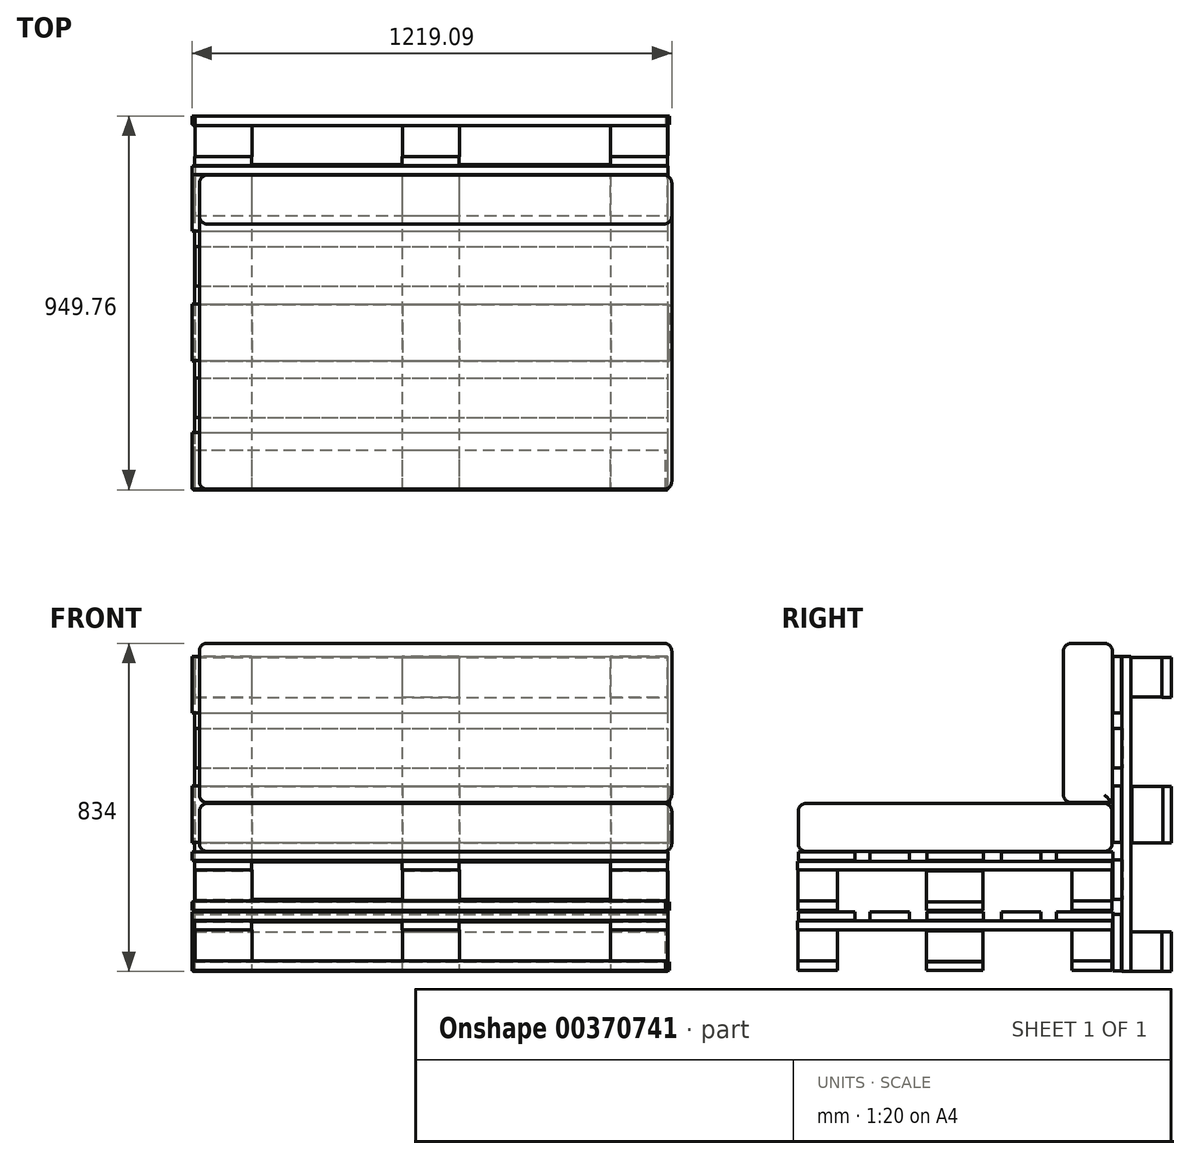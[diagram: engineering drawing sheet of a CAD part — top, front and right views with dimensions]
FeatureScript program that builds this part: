
annotation { "Feature Type Name" : "Feature", "Feature Type Description" : "" }
export const myFeature = defineFeature(function(context is Context, id is Id, definition is map)
    precondition{}
    {
        {
            var Q0;
            Q0=qCreatedBy(makeId("Top.planeOp"),FACE);
            var sketch = newSketch(context, id + "F0", { "sketchPlane" : qUnion([Q0])});
            skLineSegment(sketch, "E0.bottom", {"start": v(606.92, 402.88) * mm, "end": v(-606.52, 402.88) * mm, "construction": true});
            skLineSegment(sketch, "E0.top", {"start": v(606.92, -399.92) * mm, "end": v(-606.52, -399.92) * mm, "construction": true});
            skLineSegment(sketch, "E0.left", {"start": v(606.92, 402.88) * mm, "end": v(606.92, -399.92) * mm, "construction": true});
            skLineSegment(sketch, "E0.right", {"start": v(-606.52, 402.88) * mm, "end": v(-606.52, -399.92) * mm, "construction": true});
            skPoint(sketch, "E0.middle", {"position": v(0.2, 1.48) * mm});
            skSolve(sketch);
        }
        {
            var Q0;
            Q0=qCreatedBy(makeId("Right.planeOp"),FACE);
            var sketch = newSketch(context, id + "F1", { "sketchPlane" : qUnion([Q0])});
            skLineSegment(sketch, "E1.bottom", {"start": v(-398.91, 0) * mm, "end": v(-298, 0) * mm});
            skLineSegment(sketch, "E1.top", {"start": v(-398.91, 24.98) * mm, "end": v(-298, 24.98) * mm});
            skLineSegment(sketch, "E1.left", {"start": v(-398.91, 0) * mm, "end": v(-398.91, 24.98) * mm});
            skLineSegment(sketch, "E1.right", {"start": v(-298, 0) * mm, "end": v(-298, 24.98) * mm});
            skSolve(sketch);
        }
        {
            var Q0;
            Q0=makeQuery(id+"F1.imprint","IMPRINT",FACE,{"disambiguationData":[TD([[makeQuery(id+"F1.imprint","IMPRINT",EDGE,{"derivedFrom":sQuery(id+"F1.wireOp",EDGE,"E1.bottom")}),1.0]])]});
            extrude(context, id + "F2", {"entities" : qUnion([Q0]), "depth" : 600 * mm, "hasSecondDirection" : true, "secondDirectionOppositeDirection" : true, "secondDirectionDepth" : 600 * mm});
        }
        {
            var Q0;
            Q0=makeQuery(id+"F2.opExtrude","SWEPT_BODY",BODY,{"disambiguationData":[OSD([sQuery(id+"F1.wireOp",EDGE,"E1.bottom"),sQuery(id+"F1.wireOp",EDGE,"E1.top"),sQuery(id+"F1.wireOp",EDGE,"E1.left"),sQuery(id+"F1.wireOp",EDGE,"E1.right")])]});
            var Q1;
            Q1=qCreatedBy(makeId("Front.planeOp"),FACE);
            mirror(context, id + "F3", {"entities" : qUnion([Q0]), "mirrorPlane" : qUnion([Q1])});
        }
        {
            var Q0;
            Q0=qCreatedBy(makeId("Top.planeOp"),FACE);
            var sketch = newSketch(context, id + "F4", { "sketchPlane" : qUnion([Q0])});
            skLineSegment(sketch, "E2.bottom", {"start": v(604.9, 71.76) * mm, "end": v(-604.9, 71.76) * mm});
            skLineSegment(sketch, "E2.top", {"start": v(604.9, -71.76) * mm, "end": v(-604.9, -71.76) * mm});
            skLineSegment(sketch, "E2.left", {"start": v(604.9, 71.76) * mm, "end": v(604.9, -71.76) * mm});
            skLineSegment(sketch, "E2.right", {"start": v(-604.9, 71.76) * mm, "end": v(-604.9, -71.76) * mm});
            skPoint(sketch, "E2.middle", {"position": v(0, 0) * mm});
            skSolve(sketch);
        }
        {
            var Q0;
            Q0=makeQuery(id+"F4.imprint","IMPRINT",FACE,{"disambiguationData":[TD([[makeQuery(id+"F4.imprint","IMPRINT",EDGE,{"derivedFrom":sQuery(id+"F4.wireOp",EDGE,"E2.bottom")}),1.0]])]});
            extrude(context, id + "F5", {"entities" : qUnion([Q0]), "depth" : 22 * mm});
        }
        {
            var Q0;
            Q0=makeQuery(id+"F5.opExtrude","SWEPT_BODY",BODY,{"disambiguationData":[OSD([sQuery(id+"F4.wireOp",EDGE,"E2.bottom"),sQuery(id+"F4.wireOp",EDGE,"E2.top"),sQuery(id+"F4.wireOp",EDGE,"E2.left"),sQuery(id+"F4.wireOp",EDGE,"E2.right")])]});
            transform(context, id + "F6", {"entities" : qUnion([Q0]), "transformType" : TransformType.COPY});
        }
        {
            var Q0;
            Q0=qCreatedBy(makeId("Right.planeOp"),FACE);
            var sketch = newSketch(context, id + "F7", { "sketchPlane" : qUnion([Q0])});
            skLineSegment(sketch, "E3.bottom", {"start": v(398.94, 24.94) * mm, "end": v(297.72, 24.94) * mm});
            skLineSegment(sketch, "E3.top", {"start": v(398.94, 103.56) * mm, "end": v(297.72, 103.56) * mm});
            skLineSegment(sketch, "E3.left", {"start": v(398.94, 24.94) * mm, "end": v(398.94, 103.56) * mm});
            skLineSegment(sketch, "E3.right", {"start": v(297.72, 24.94) * mm, "end": v(297.72, 103.56) * mm});
            skSolve(sketch);
        }
        {
            var Q0;
            Q0=makeQuery(id+"F7.imprint","IMPRINT",FACE,{"disambiguationData":[TD([[makeQuery(id+"F7.imprint","IMPRINT",EDGE,{"derivedFrom":sQuery(id+"F7.wireOp",EDGE,"E3.bottom")}),-1.0]])]});
            extrude(context, id + "F8", {"entities" : qUnion([Q0]), "depth" : 145 * mm});
        }
        {
            var Q0;
            Q0=makeQuery(id+"F8.opExtrude","SWEPT_BODY",BODY,{"disambiguationData":[OSD([sQuery(id+"F7.wireOp",EDGE,"E3.bottom"),sQuery(id+"F7.wireOp",EDGE,"E3.top"),sQuery(id+"F7.wireOp",EDGE,"E3.left"),sQuery(id+"F7.wireOp",EDGE,"E3.right")])]});
            var Q1;
            Q1=sQuery(id+"F0.wireOp",EDGE,"E0.top");
            transform(context, id + "F9", {"entities" : qUnion([Q0]), "transformType" : TransformType.TRANSLATION_DISTANCE, "transformDirection" : qUnion([Q1]), "distance" : 455 * mm, "oppositeDirection" : true, "makeCopy" : false});
        }
        {
            var Q0;
            Q0=makeQuery(id+"F8.opExtrude","SWEPT_BODY",BODY,{"disambiguationData":[OSD([sQuery(id+"F7.wireOp",EDGE,"E3.bottom"),sQuery(id+"F7.wireOp",EDGE,"E3.top"),sQuery(id+"F7.wireOp",EDGE,"E3.left"),sQuery(id+"F7.wireOp",EDGE,"E3.right")])]});
            var Q1;
            Q1=makeQuery(id+"F3.opPattern","COPY",EDGE,{"derivedFrom":makeQuery(id+"F2.opExtrude","SWEPT_EDGE",EDGE,{"disambiguationData":[OSD([sQuery(id+"F1.wireOp",EDGE,"E1.top"),sQuery(id+"F1.wireOp",EDGE,"E1.left")])]}),"instanceName":"1"});
            transform(context, id + "F10", {"entities" : qUnion([Q0]), "transformType" : TransformType.TRANSLATION_DISTANCE, "transformDirection" : qUnion([Q1]), "distance" : 1055 * mm, "makeCopy" : true});
        }
        {
            var Q0;
            Q0=makeQuery(id+"F8.opExtrude","SWEPT_BODY",BODY,{"disambiguationData":[OSD([sQuery(id+"F7.wireOp",EDGE,"E3.bottom"),sQuery(id+"F7.wireOp",EDGE,"E3.top"),sQuery(id+"F7.wireOp",EDGE,"E3.left"),sQuery(id+"F7.wireOp",EDGE,"E3.right")])]});
            var Q1;
            Q1=makeQuery(id+"F3.opPattern","COPY",BODY,{"derivedFrom":makeQuery(id+"F2.opExtrude","SWEPT_BODY",BODY,{"disambiguationData":[OSD([sQuery(id+"F1.wireOp",EDGE,"E1.bottom"),sQuery(id+"F1.wireOp",EDGE,"E1.top"),sQuery(id+"F1.wireOp",EDGE,"E1.left"),sQuery(id+"F1.wireOp",EDGE,"E1.right")])]}),"instanceName":"1"});
            var Q2;
            Q2=makeQuery(id+"F3.opPattern","COPY",EDGE,{"derivedFrom":makeQuery(id+"F2.opExtrude","SWEPT_EDGE",EDGE,{"disambiguationData":[OSD([sQuery(id+"F1.wireOp",EDGE,"E1.top"),sQuery(id+"F1.wireOp",EDGE,"E1.left")])]}),"instanceName":"1"});
            transform(context, id + "F11", {"entities" : qUnion([Q0, Q1]), "transformType" : TransformType.TRANSLATION_DISTANCE, "transformDirection" : qUnion([Q2]), "distance" : 527 * mm, "makeCopy" : true});
        }
        {
            var Q0;
            Q0=makeQuery(id+"F11.opPattern","COPY",BODY,{"derivedFrom":makeQuery(id+"F3.opPattern","COPY",BODY,{"derivedFrom":makeQuery(id+"F2.opExtrude","SWEPT_BODY",BODY,{"disambiguationData":[OSD([sQuery(id+"F1.wireOp",EDGE,"E1.bottom"),sQuery(id+"F1.wireOp",EDGE,"E1.top"),sQuery(id+"F1.wireOp",EDGE,"E1.left"),sQuery(id+"F1.wireOp",EDGE,"E1.right")])]}),"instanceName":"1"}),"instanceName":"1"});
            deleteBodies(context, id + "F12", {"entities" : qUnion([Q0])});
        }
        {
            var Q0;
            Q0=makeQuery(id+"F8.opExtrude","SWEPT_BODY",BODY,{"disambiguationData":[OSD([sQuery(id+"F7.wireOp",EDGE,"E3.bottom"),sQuery(id+"F7.wireOp",EDGE,"E3.top"),sQuery(id+"F7.wireOp",EDGE,"E3.left"),sQuery(id+"F7.wireOp",EDGE,"E3.right")])]});
            var Q1;
            Q1=makeQuery(id+"F11.opPattern","COPY",BODY,{"derivedFrom":makeQuery(id+"F8.opExtrude","SWEPT_BODY",BODY,{"disambiguationData":[OSD([sQuery(id+"F7.wireOp",EDGE,"E3.bottom"),sQuery(id+"F7.wireOp",EDGE,"E3.top"),sQuery(id+"F7.wireOp",EDGE,"E3.left"),sQuery(id+"F7.wireOp",EDGE,"E3.right")])]}),"instanceName":"1"});
            var Q2;
            Q2=makeQuery(id+"F10.opPattern","COPY",BODY,{"derivedFrom":makeQuery(id+"F8.opExtrude","SWEPT_BODY",BODY,{"disambiguationData":[OSD([sQuery(id+"F7.wireOp",EDGE,"E3.bottom"),sQuery(id+"F7.wireOp",EDGE,"E3.top"),sQuery(id+"F7.wireOp",EDGE,"E3.left"),sQuery(id+"F7.wireOp",EDGE,"E3.right")])]}),"instanceName":"1"});
            var Q3;
            Q3=makeQuery(id+"F5.opExtrude","CAP_EDGE",EDGE,{"disambiguationData":[OSD([sQuery(id+"F4.wireOp",EDGE,"E2.right")])],"isStart":false});
            transform(context, id + "F13", {"entities" : qUnion([Q0, Q1, Q2]), "transformType" : TransformType.TRANSLATION_DISTANCE, "transformDirection" : qUnion([Q3]), "distance" : 697 * mm, "makeCopy" : true});
        }
        {
            var Q0;
            Q0=qCreatedBy(makeId("Right.planeOp"),FACE);
            var sketch = newSketch(context, id + "F14", { "sketchPlane" : qUnion([Q0])});
            skLineSegment(sketch, "E4.bottom", {"start": v(-71.96, 39.25) * mm, "end": v(71.96, 39.25) * mm});
            skLineSegment(sketch, "E4.top", {"start": v(-71.96, -39.25) * mm, "end": v(71.96, -39.25) * mm});
            skLineSegment(sketch, "E4.left", {"start": v(-71.96, 39.25) * mm, "end": v(-71.96, -39.25) * mm});
            skLineSegment(sketch, "E4.right", {"start": v(71.96, 39.25) * mm, "end": v(71.96, -39.25) * mm});
            skPoint(sketch, "E4.middle", {"position": v(0, 0) * mm});
            skSolve(sketch);
        }
        {
            var Q0;
            Q0=makeQuery(id+"F14.imprint","IMPRINT",FACE,{"disambiguationData":[TD([[makeQuery(id+"F14.imprint","IMPRINT",EDGE,{"derivedFrom":sQuery(id+"F14.wireOp",EDGE,"E4.bottom")}),-1.0]])]});
            extrude(context, id + "F15", {"entities" : qUnion([Q0]), "depth" : 145 * mm});
        }
        {
            var Q0;
            Q0=makeQuery(id+"F15.opExtrude","SWEPT_BODY",BODY,{"disambiguationData":[OSD([sQuery(id+"F14.wireOp",EDGE,"E4.bottom"),sQuery(id+"F14.wireOp",EDGE,"E4.top"),sQuery(id+"F14.wireOp",EDGE,"E4.left"),sQuery(id+"F14.wireOp",EDGE,"E4.right")])]});
            var Q1;
            Q1=makeQuery(id+"F13.opPattern","COPY",EDGE,{"derivedFrom":makeQuery(id+"F11.opPattern","COPY",EDGE,{"derivedFrom":makeQuery(id+"F8.opExtrude","CAP_EDGE",EDGE,{"disambiguationData":[OSD([sQuery(id+"F7.wireOp",EDGE,"E3.left")])],"isStart":false}),"instanceName":"1"}),"instanceName":"1"});
            transform(context, id + "F16", {"entities" : qUnion([Q0]), "transformType" : TransformType.TRANSLATION_DISTANCE, "transformDirection" : qUnion([Q1]), "distance" : 61.8 * mm, "makeCopy" : false});
        }
        {
            var Q0;
            Q0=makeQuery(id+"F15.opExtrude","SWEPT_BODY",BODY,{"disambiguationData":[OSD([sQuery(id+"F14.wireOp",EDGE,"E4.bottom"),sQuery(id+"F14.wireOp",EDGE,"E4.top"),sQuery(id+"F14.wireOp",EDGE,"E4.left"),sQuery(id+"F14.wireOp",EDGE,"E4.right")])]});
            var Q1;
            Q1=makeQuery(id+"F3.opPattern","COPY",BODY,{"derivedFrom":makeQuery(id+"F2.opExtrude","SWEPT_BODY",BODY,{"disambiguationData":[OSD([sQuery(id+"F1.wireOp",EDGE,"E1.bottom"),sQuery(id+"F1.wireOp",EDGE,"E1.top"),sQuery(id+"F1.wireOp",EDGE,"E1.left"),sQuery(id+"F1.wireOp",EDGE,"E1.right")])]}),"instanceName":"1"});
            var Q2;
            Q2=makeQuery(id+"F3.opPattern","COPY",EDGE,{"derivedFrom":makeQuery(id+"F2.opExtrude","SWEPT_EDGE",EDGE,{"disambiguationData":[OSD([sQuery(id+"F1.wireOp",EDGE,"E1.top"),sQuery(id+"F1.wireOp",EDGE,"E1.left")])]}),"instanceName":"1"});
            transform(context, id + "F17", {"entities" : qUnion([Q0, Q1]), "transformType" : TransformType.TRANSLATION_DISTANCE, "transformDirection" : qUnion([Q2]), "distance" : 72.6 * mm, "makeCopy" : false});
        }
        {
            var Q0;
            Q0=makeQuery(id+"F3.opPattern","COPY",BODY,{"derivedFrom":makeQuery(id+"F2.opExtrude","SWEPT_BODY",BODY,{"disambiguationData":[OSD([sQuery(id+"F1.wireOp",EDGE,"E1.bottom"),sQuery(id+"F1.wireOp",EDGE,"E1.top"),sQuery(id+"F1.wireOp",EDGE,"E1.left"),sQuery(id+"F1.wireOp",EDGE,"E1.right")])]}),"instanceName":"1"});
            var Q1;
            Q1=makeQuery(id+"F3.opPattern","COPY",EDGE,{"derivedFrom":makeQuery(id+"F2.opExtrude","SWEPT_EDGE",EDGE,{"disambiguationData":[OSD([sQuery(id+"F1.wireOp",EDGE,"E1.top"),sQuery(id+"F1.wireOp",EDGE,"E1.left")])]}),"instanceName":"1"});
            transform(context, id + "F18", {"entities" : qUnion([Q0]), "transformType" : TransformType.TRANSLATION_DISTANCE, "transformDirection" : qUnion([Q1]), "distance" : 77 * mm, "oppositeDirection" : true, "makeCopy" : false});
        }
        {
            var Q0;
            Q0=makeQuery(id+"F15.opExtrude","SWEPT_BODY",BODY,{"disambiguationData":[OSD([sQuery(id+"F14.wireOp",EDGE,"E4.bottom"),sQuery(id+"F14.wireOp",EDGE,"E4.top"),sQuery(id+"F14.wireOp",EDGE,"E4.left"),sQuery(id+"F14.wireOp",EDGE,"E4.right")])]});
            var Q1;
            Q1=makeQuery(id+"F5.opExtrude","CAP_EDGE",EDGE,{"disambiguationData":[OSD([sQuery(id+"F4.wireOp",EDGE,"E2.bottom")])],"isStart":false});
            transform(context, id + "F19", {"entities" : qUnion([Q0]), "transformType" : TransformType.TRANSLATION_DISTANCE, "transformDirection" : qUnion([Q1]), "distance" : 534 * mm, "oppositeDirection" : true, "makeCopy" : true});
        }
        {
            var Q0;
            Q0=makeQuery(id+"F15.opExtrude","SWEPT_BODY",BODY,{"disambiguationData":[OSD([sQuery(id+"F14.wireOp",EDGE,"E4.bottom"),sQuery(id+"F14.wireOp",EDGE,"E4.top"),sQuery(id+"F14.wireOp",EDGE,"E4.left"),sQuery(id+"F14.wireOp",EDGE,"E4.right")])]});
            var Q1;
            Q1=makeQuery(id+"F5.opExtrude","CAP_EDGE",EDGE,{"disambiguationData":[OSD([sQuery(id+"F4.wireOp",EDGE,"E2.bottom")])],"isStart":false});
            transform(context, id + "F20", {"entities" : qUnion([Q0]), "transformType" : TransformType.TRANSLATION_DISTANCE, "transformDirection" : qUnion([Q1]), "distance" : 532 * mm, "makeCopy" : true});
        }
        {
            var Q0;
            Q0=makeQuery(id+"F5.opExtrude","SWEPT_BODY",BODY,{"disambiguationData":[OSD([sQuery(id+"F4.wireOp",EDGE,"E2.bottom"),sQuery(id+"F4.wireOp",EDGE,"E2.top"),sQuery(id+"F4.wireOp",EDGE,"E2.left"),sQuery(id+"F4.wireOp",EDGE,"E2.right")])]});
            var Q1;
            Q1=makeQuery(id+"F20.opPattern","COPY",BODY,{"derivedFrom":makeQuery(id+"F15.opExtrude","SWEPT_BODY",BODY,{"disambiguationData":[OSD([sQuery(id+"F14.wireOp",EDGE,"E4.bottom"),sQuery(id+"F14.wireOp",EDGE,"E4.top"),sQuery(id+"F14.wireOp",EDGE,"E4.left"),sQuery(id+"F14.wireOp",EDGE,"E4.right")])]}),"instanceName":"1"});
            var Q2;
            Q2=makeQuery(id+"F2.opExtrude","SWEPT_EDGE",EDGE,{"disambiguationData":[OSD([sQuery(id+"F1.wireOp",EDGE,"E1.top"),sQuery(id+"F1.wireOp",EDGE,"E1.left")])]});
            transform(context, id + "F21", {"entities" : qUnion([Q0, Q1]), "transformType" : TransformType.TRANSLATION_DISTANCE, "transformDirection" : qUnion([Q2]), "distance" : 3 * mm, "oppositeDirection" : true, "makeCopy" : false});
        }
        {
            var Q0;
            Q0=qCreatedBy(makeId("Front.planeOp"),FACE);
            var sketch = newSketch(context, id + "F22", { "sketchPlane" : qUnion([Q0])});
            skLineSegment(sketch, "E5.bottom", {"start": v(-600.02, 103.6) * mm, "end": v(-455.57, 103.6) * mm});
            skLineSegment(sketch, "E5.top", {"start": v(-600.02, 125.7) * mm, "end": v(-455.57, 125.7) * mm});
            skLineSegment(sketch, "E5.left", {"start": v(-600.02, 103.6) * mm, "end": v(-600.02, 125.7) * mm});
            skLineSegment(sketch, "E5.right", {"start": v(-455.57, 103.6) * mm, "end": v(-455.57, 125.7) * mm});
            skSolve(sketch);
        }
        {
            var Q0;
            Q0=makeQuery(id+"F22.imprint","IMPRINT",FACE,{"disambiguationData":[TD([[makeQuery(id+"F22.imprint","IMPRINT",EDGE,{"derivedFrom":sQuery(id+"F22.wireOp",EDGE,"E5.bottom")}),1.0]])]});
            extrude(context, id + "F23", {"entities" : qUnion([Q0]), "depth" : 401 * mm, "hasSecondDirection" : true, "secondDirectionOppositeDirection" : true, "secondDirectionDepth" : 399 * mm});
        }
        {
            var Q0;
            Q0=makeQuery(id+"F23.opExtrude","SWEPT_BODY",BODY,{"disambiguationData":[OSD([sQuery(id+"F22.wireOp",EDGE,"E5.bottom"),sQuery(id+"F22.wireOp",EDGE,"E5.top"),sQuery(id+"F22.wireOp",EDGE,"E5.left"),sQuery(id+"F22.wireOp",EDGE,"E5.right")])]});
            var Q1;
            Q1=makeQuery(id+"F2.opExtrude","SWEPT_EDGE",EDGE,{"disambiguationData":[OSD([sQuery(id+"F1.wireOp",EDGE,"E1.top"),sQuery(id+"F1.wireOp",EDGE,"E1.left")])]});
            transform(context, id + "F24", {"entities" : qUnion([Q0]), "transformType" : TransformType.TRANSLATION_DISTANCE, "transformDirection" : qUnion([Q1]), "distance" : 529 * mm, "oppositeDirection" : true, "makeCopy" : true});
        }
        {
            var Q0;
            Q0=makeQuery(id+"F24.opPattern","COPY",BODY,{"derivedFrom":makeQuery(id+"F23.opExtrude","SWEPT_BODY",BODY,{"disambiguationData":[OSD([sQuery(id+"F22.wireOp",EDGE,"E5.bottom"),sQuery(id+"F22.wireOp",EDGE,"E5.top"),sQuery(id+"F22.wireOp",EDGE,"E5.left"),sQuery(id+"F22.wireOp",EDGE,"E5.right")])]}),"instanceName":"1"});
            var Q1;
            Q1=makeQuery(id+"F2.opExtrude","SWEPT_EDGE",EDGE,{"disambiguationData":[OSD([sQuery(id+"F1.wireOp",EDGE,"E1.top"),sQuery(id+"F1.wireOp",EDGE,"E1.left")])]});
            transform(context, id + "F25", {"entities" : qUnion([Q0]), "transformType" : TransformType.TRANSLATION_DISTANCE, "transformDirection" : qUnion([Q1]), "distance" : 527 * mm, "oppositeDirection" : true, "makeCopy" : true});
        }
        {
            var Q0;
            Q0=makeQuery(id+"F19.opPattern","COPY",BODY,{"derivedFrom":makeQuery(id+"F15.opExtrude","SWEPT_BODY",BODY,{"disambiguationData":[OSD([sQuery(id+"F14.wireOp",EDGE,"E4.bottom"),sQuery(id+"F14.wireOp",EDGE,"E4.top"),sQuery(id+"F14.wireOp",EDGE,"E4.left"),sQuery(id+"F14.wireOp",EDGE,"E4.right")])]}),"instanceName":"1"});
            var Q1;
            Q1=makeQuery(id+"F2.opExtrude","SWEPT_EDGE",EDGE,{"disambiguationData":[OSD([sQuery(id+"F1.wireOp",EDGE,"E1.top"),sQuery(id+"F1.wireOp",EDGE,"E1.left")])]});
            transform(context, id + "F26", {"entities" : qUnion([Q0]), "transformType" : TransformType.TRANSLATION_DISTANCE, "transformDirection" : qUnion([Q1]), "distance" : 7 * mm, "makeCopy" : false});
        }
        {
            var Q0;
            Q0=makeQuery(id+"F5.opExtrude","SWEPT_BODY",BODY,{"disambiguationData":[OSD([sQuery(id+"F4.wireOp",EDGE,"E2.bottom"),sQuery(id+"F4.wireOp",EDGE,"E2.top"),sQuery(id+"F4.wireOp",EDGE,"E2.left"),sQuery(id+"F4.wireOp",EDGE,"E2.right")])]});
            var Q1;
            Q1=makeQuery(id+"F19.opPattern","COPY",EDGE,{"derivedFrom":makeQuery(id+"F15.opExtrude","CAP_EDGE",EDGE,{"disambiguationData":[OSD([sQuery(id+"F14.wireOp",EDGE,"E4.left")])],"isStart":false}),"instanceName":"1"});
            transform(context, id + "F27", {"entities" : qUnion([Q0]), "transformType" : TransformType.TRANSLATION_DISTANCE, "transformDirection" : qUnion([Q1]), "distance" : 127 * mm, "oppositeDirection" : true, "makeCopy" : true});
        }
        {
            var Q0;
            Q0=makeQuery(id+"F27.opPattern","COPY",BODY,{"derivedFrom":makeQuery(id+"F5.opExtrude","SWEPT_BODY",BODY,{"disambiguationData":[OSD([sQuery(id+"F4.wireOp",EDGE,"E2.bottom"),sQuery(id+"F4.wireOp",EDGE,"E2.top"),sQuery(id+"F4.wireOp",EDGE,"E2.left"),sQuery(id+"F4.wireOp",EDGE,"E2.right")])]}),"instanceName":"1"});
            var Q1;
            Q1=makeQuery(id+"F25.opPattern","COPY",EDGE,{"derivedFrom":makeQuery(id+"F24.opPattern","COPY",EDGE,{"derivedFrom":makeQuery(id+"F23.opExtrude","SWEPT_EDGE",EDGE,{"disambiguationData":[OSD([sQuery(id+"F22.wireOp",EDGE,"E5.top"),sQuery(id+"F22.wireOp",EDGE,"E5.right")])]}),"instanceName":"1"}),"instanceName":"1"});
            transform(context, id + "F28", {"entities" : qUnion([Q0]), "transformType" : TransformType.TRANSLATION_DISTANCE, "transformDirection" : qUnion([Q1]), "distance" : 330 * mm, "oppositeDirection" : true, "makeCopy" : false});
        }
        {
            var Q0;
            Q0=makeQuery(id+"F27.opPattern","COPY",BODY,{"derivedFrom":makeQuery(id+"F5.opExtrude","SWEPT_BODY",BODY,{"disambiguationData":[OSD([sQuery(id+"F4.wireOp",EDGE,"E2.bottom"),sQuery(id+"F4.wireOp",EDGE,"E2.top"),sQuery(id+"F4.wireOp",EDGE,"E2.left"),sQuery(id+"F4.wireOp",EDGE,"E2.right")])]}),"instanceName":"1"});
            var Q1;
            Q1=makeQuery(id+"F25.opPattern","COPY",EDGE,{"derivedFrom":makeQuery(id+"F24.opPattern","COPY",EDGE,{"derivedFrom":makeQuery(id+"F23.opExtrude","SWEPT_EDGE",EDGE,{"disambiguationData":[OSD([sQuery(id+"F22.wireOp",EDGE,"E5.top"),sQuery(id+"F22.wireOp",EDGE,"E5.right")])]}),"instanceName":"1"}),"instanceName":"1"});
            transform(context, id + "F29", {"entities" : qUnion([Q0]), "transformType" : TransformType.TRANSLATION_DISTANCE, "transformDirection" : qUnion([Q1]), "distance" : 655 * mm, "makeCopy" : true});
        }
        {
            var Q0;
            Q0=makeQuery(id+"F29.opPattern","COPY",BODY,{"derivedFrom":makeQuery(id+"F27.opPattern","COPY",BODY,{"derivedFrom":makeQuery(id+"F5.opExtrude","SWEPT_BODY",BODY,{"disambiguationData":[OSD([sQuery(id+"F4.wireOp",EDGE,"E2.bottom"),sQuery(id+"F4.wireOp",EDGE,"E2.top"),sQuery(id+"F4.wireOp",EDGE,"E2.left"),sQuery(id+"F4.wireOp",EDGE,"E2.right")])]}),"instanceName":"1"}),"instanceName":"1"});
            var Q1;
            Q1=makeQuery(id+"F25.opPattern","COPY",EDGE,{"derivedFrom":makeQuery(id+"F24.opPattern","COPY",EDGE,{"derivedFrom":makeQuery(id+"F23.opExtrude","SWEPT_EDGE",EDGE,{"disambiguationData":[OSD([sQuery(id+"F22.wireOp",EDGE,"E5.top"),sQuery(id+"F22.wireOp",EDGE,"E5.right")])]}),"instanceName":"1"}),"instanceName":"1"});
            transform(context, id + "F30", {"entities" : qUnion([Q0]), "transformType" : TransformType.TRANSLATION_DISTANCE, "transformDirection" : qUnion([Q1]), "distance" : 326 * mm, "oppositeDirection" : true, "makeCopy" : true});
        }
        {
            var Q0;
            Q0=makeQuery(id+"F2.opExtrude","SWEPT_BODY",BODY,{"disambiguationData":[OSD([sQuery(id+"F1.wireOp",EDGE,"E1.bottom"),sQuery(id+"F1.wireOp",EDGE,"E1.top"),sQuery(id+"F1.wireOp",EDGE,"E1.left"),sQuery(id+"F1.wireOp",EDGE,"E1.right")])]});
            transform(context, id + "F31", {"entities" : qUnion([Q0]), "transformType" : TransformType.TRANSLATION_3D, "dx" : 0 * mm, "dy" : 180 * mm, "dz" : 125 * mm, "makeCopy" : true});
        }
        {
            var Q0;
            Q0=makeQuery(id+"F31.opPattern","COPY",BODY,{"derivedFrom":makeQuery(id+"F2.opExtrude","SWEPT_BODY",BODY,{"disambiguationData":[OSD([sQuery(id+"F1.wireOp",EDGE,"E1.bottom"),sQuery(id+"F1.wireOp",EDGE,"E1.top"),sQuery(id+"F1.wireOp",EDGE,"E1.left"),sQuery(id+"F1.wireOp",EDGE,"E1.right")])]}),"instanceName":"1"});
            var Q1;
            Q1=makeQuery(id+"F30.opPattern","COPY",EDGE,{"derivedFrom":makeQuery(id+"F29.opPattern","COPY",EDGE,{"derivedFrom":makeQuery(id+"F27.opPattern","COPY",EDGE,{"derivedFrom":makeQuery(id+"F5.opExtrude","SWEPT_EDGE",EDGE,{"disambiguationData":[OSD([sQuery(id+"F4.wireOp",EDGE,"E2.top"),sQuery(id+"F4.wireOp",EDGE,"E2.left")])]}),"instanceName":"1"}),"instanceName":"1"}),"instanceName":"1"});
            transform(context, id + "F32", {"entities" : qUnion([Q0]), "transformType" : TransformType.TRANSLATION_DISTANCE, "transformDirection" : qUnion([Q1]), "distance" : 1 * mm, "oppositeDirection" : true, "makeCopy" : false});
        }
        {
            var Q0;
            Q0=makeQuery(id+"F31.opPattern","COPY",BODY,{"derivedFrom":makeQuery(id+"F2.opExtrude","SWEPT_BODY",BODY,{"disambiguationData":[OSD([sQuery(id+"F1.wireOp",EDGE,"E1.bottom"),sQuery(id+"F1.wireOp",EDGE,"E1.top"),sQuery(id+"F1.wireOp",EDGE,"E1.left"),sQuery(id+"F1.wireOp",EDGE,"E1.right")])]}),"instanceName":"1"});
            var Q1;
            Q1=makeQuery(id+"F25.opPattern","COPY",EDGE,{"derivedFrom":makeQuery(id+"F24.opPattern","COPY",EDGE,{"derivedFrom":makeQuery(id+"F23.opExtrude","SWEPT_EDGE",EDGE,{"disambiguationData":[OSD([sQuery(id+"F22.wireOp",EDGE,"E5.top"),sQuery(id+"F22.wireOp",EDGE,"E5.right")])]}),"instanceName":"1"}),"instanceName":"1"});
            transform(context, id + "F33", {"entities" : qUnion([Q0]), "transformType" : TransformType.TRANSLATION_DISTANCE, "transformDirection" : qUnion([Q1]), "distance" : 334 * mm, "makeCopy" : true});
        }
        {
            var Q0;
            Q0=makeQuery(id+"F31.opPattern","COPY",BODY,{"derivedFrom":makeQuery(id+"F2.opExtrude","SWEPT_BODY",BODY,{"disambiguationData":[OSD([sQuery(id+"F1.wireOp",EDGE,"E1.bottom"),sQuery(id+"F1.wireOp",EDGE,"E1.top"),sQuery(id+"F1.wireOp",EDGE,"E1.left"),sQuery(id+"F1.wireOp",EDGE,"E1.right")])]}),"instanceName":"1"});
            var Q1;
            Q1=makeQuery(id+"F33.opPattern","COPY",BODY,{"derivedFrom":makeQuery(id+"F31.opPattern","COPY",BODY,{"derivedFrom":makeQuery(id+"F2.opExtrude","SWEPT_BODY",BODY,{"disambiguationData":[OSD([sQuery(id+"F1.wireOp",EDGE,"E1.bottom"),sQuery(id+"F1.wireOp",EDGE,"E1.top"),sQuery(id+"F1.wireOp",EDGE,"E1.left"),sQuery(id+"F1.wireOp",EDGE,"E1.right")])]}),"instanceName":"1"}),"instanceName":"1"});
            var Q2;
            Q2=makeQuery(id+"F30.opPattern","COPY",EDGE,{"derivedFrom":makeQuery(id+"F29.opPattern","COPY",EDGE,{"derivedFrom":makeQuery(id+"F27.opPattern","COPY",EDGE,{"derivedFrom":makeQuery(id+"F5.opExtrude","SWEPT_EDGE",EDGE,{"disambiguationData":[OSD([sQuery(id+"F4.wireOp",EDGE,"E2.bottom"),sQuery(id+"F4.wireOp",EDGE,"E2.left")])]}),"instanceName":"1"}),"instanceName":"1"}),"instanceName":"1"});
            transform(context, id + "F34", {"entities" : qUnion([Q0, Q1]), "transformType" : TransformType.TRANSLATION_DISTANCE, "transformDirection" : qUnion([Q2]), "distance" : 2 * mm, "makeCopy" : false});
        }
        {
            var Q0;
            Q0=makeQuery(id+"F2.opExtrude","SWEPT_BODY",BODY,{"disambiguationData":[OSD([sQuery(id+"F1.wireOp",EDGE,"E1.bottom"),sQuery(id+"F1.wireOp",EDGE,"E1.top"),sQuery(id+"F1.wireOp",EDGE,"E1.left"),sQuery(id+"F1.wireOp",EDGE,"E1.right")])]});
            var Q1;
            Q1=makeQuery(id+"F3.opPattern","COPY",BODY,{"derivedFrom":makeQuery(id+"F2.opExtrude","SWEPT_BODY",BODY,{"disambiguationData":[OSD([sQuery(id+"F1.wireOp",EDGE,"E1.bottom"),sQuery(id+"F1.wireOp",EDGE,"E1.top"),sQuery(id+"F1.wireOp",EDGE,"E1.left"),sQuery(id+"F1.wireOp",EDGE,"E1.right")])]}),"instanceName":"1"});
            var Q2;
            Q2=makeQuery(id+"F25.opPattern","COPY",BODY,{"derivedFrom":makeQuery(id+"F24.opPattern","COPY",BODY,{"derivedFrom":makeQuery(id+"F23.opExtrude","SWEPT_BODY",BODY,{"disambiguationData":[OSD([sQuery(id+"F22.wireOp",EDGE,"E5.bottom"),sQuery(id+"F22.wireOp",EDGE,"E5.top"),sQuery(id+"F22.wireOp",EDGE,"E5.left"),sQuery(id+"F22.wireOp",EDGE,"E5.right")])]}),"instanceName":"1"}),"instanceName":"1"});
            var Q3;
            Q3=makeQuery(id+"F13.opPattern","COPY",BODY,{"derivedFrom":makeQuery(id+"F8.opExtrude","SWEPT_BODY",BODY,{"disambiguationData":[OSD([sQuery(id+"F7.wireOp",EDGE,"E3.bottom"),sQuery(id+"F7.wireOp",EDGE,"E3.top"),sQuery(id+"F7.wireOp",EDGE,"E3.left"),sQuery(id+"F7.wireOp",EDGE,"E3.right")])]}),"instanceName":"1"});
            var Q4;
            Q4=makeQuery(id+"F27.opPattern","COPY",BODY,{"derivedFrom":makeQuery(id+"F5.opExtrude","SWEPT_BODY",BODY,{"disambiguationData":[OSD([sQuery(id+"F4.wireOp",EDGE,"E2.bottom"),sQuery(id+"F4.wireOp",EDGE,"E2.top"),sQuery(id+"F4.wireOp",EDGE,"E2.left"),sQuery(id+"F4.wireOp",EDGE,"E2.right")])]}),"instanceName":"1"});
            var Q5;
            Q5=makeQuery(id+"F8.opExtrude","SWEPT_BODY",BODY,{"disambiguationData":[OSD([sQuery(id+"F7.wireOp",EDGE,"E3.bottom"),sQuery(id+"F7.wireOp",EDGE,"E3.top"),sQuery(id+"F7.wireOp",EDGE,"E3.left"),sQuery(id+"F7.wireOp",EDGE,"E3.right")])]});
            var Q6;
            Q6=makeQuery(id+"F5.opExtrude","SWEPT_BODY",BODY,{"disambiguationData":[OSD([sQuery(id+"F4.wireOp",EDGE,"E2.bottom"),sQuery(id+"F4.wireOp",EDGE,"E2.top"),sQuery(id+"F4.wireOp",EDGE,"E2.left"),sQuery(id+"F4.wireOp",EDGE,"E2.right")])]});
            var Q7;
            Q7=makeQuery(id+"F31.opPattern","COPY",BODY,{"derivedFrom":makeQuery(id+"F2.opExtrude","SWEPT_BODY",BODY,{"disambiguationData":[OSD([sQuery(id+"F1.wireOp",EDGE,"E1.bottom"),sQuery(id+"F1.wireOp",EDGE,"E1.top"),sQuery(id+"F1.wireOp",EDGE,"E1.left"),sQuery(id+"F1.wireOp",EDGE,"E1.right")])]}),"instanceName":"1"});
            var Q8;
            Q8=makeQuery(id+"F29.opPattern","COPY",BODY,{"derivedFrom":makeQuery(id+"F27.opPattern","COPY",BODY,{"derivedFrom":makeQuery(id+"F5.opExtrude","SWEPT_BODY",BODY,{"disambiguationData":[OSD([sQuery(id+"F4.wireOp",EDGE,"E2.bottom"),sQuery(id+"F4.wireOp",EDGE,"E2.top"),sQuery(id+"F4.wireOp",EDGE,"E2.left"),sQuery(id+"F4.wireOp",EDGE,"E2.right")])]}),"instanceName":"1"}),"instanceName":"1"});
            var Q9;
            Q9=makeQuery(id+"F19.opPattern","COPY",BODY,{"derivedFrom":makeQuery(id+"F15.opExtrude","SWEPT_BODY",BODY,{"disambiguationData":[OSD([sQuery(id+"F14.wireOp",EDGE,"E4.bottom"),sQuery(id+"F14.wireOp",EDGE,"E4.top"),sQuery(id+"F14.wireOp",EDGE,"E4.left"),sQuery(id+"F14.wireOp",EDGE,"E4.right")])]}),"instanceName":"1"});
            var Q10;
            Q10=makeQuery(id+"F30.opPattern","COPY",BODY,{"derivedFrom":makeQuery(id+"F29.opPattern","COPY",BODY,{"derivedFrom":makeQuery(id+"F27.opPattern","COPY",BODY,{"derivedFrom":makeQuery(id+"F5.opExtrude","SWEPT_BODY",BODY,{"disambiguationData":[OSD([sQuery(id+"F4.wireOp",EDGE,"E2.bottom"),sQuery(id+"F4.wireOp",EDGE,"E2.top"),sQuery(id+"F4.wireOp",EDGE,"E2.left"),sQuery(id+"F4.wireOp",EDGE,"E2.right")])]}),"instanceName":"1"}),"instanceName":"1"}),"instanceName":"1"});
            var Q11;
            Q11=makeQuery(id+"F33.opPattern","COPY",BODY,{"derivedFrom":makeQuery(id+"F31.opPattern","COPY",BODY,{"derivedFrom":makeQuery(id+"F2.opExtrude","SWEPT_BODY",BODY,{"disambiguationData":[OSD([sQuery(id+"F1.wireOp",EDGE,"E1.bottom"),sQuery(id+"F1.wireOp",EDGE,"E1.top"),sQuery(id+"F1.wireOp",EDGE,"E1.left"),sQuery(id+"F1.wireOp",EDGE,"E1.right")])]}),"instanceName":"1"}),"instanceName":"1"});
            var Q12;
            Q12=makeQuery(id+"F6.opPattern","COPY",BODY,{"derivedFrom":makeQuery(id+"F5.opExtrude","SWEPT_BODY",BODY,{"disambiguationData":[OSD([sQuery(id+"F4.wireOp",EDGE,"E2.bottom"),sQuery(id+"F4.wireOp",EDGE,"E2.top"),sQuery(id+"F4.wireOp",EDGE,"E2.left"),sQuery(id+"F4.wireOp",EDGE,"E2.right")])]}),"instanceName":"1"});
            var Q13;
            Q13=makeQuery(id+"F24.opPattern","COPY",BODY,{"derivedFrom":makeQuery(id+"F23.opExtrude","SWEPT_BODY",BODY,{"disambiguationData":[OSD([sQuery(id+"F22.wireOp",EDGE,"E5.bottom"),sQuery(id+"F22.wireOp",EDGE,"E5.top"),sQuery(id+"F22.wireOp",EDGE,"E5.left"),sQuery(id+"F22.wireOp",EDGE,"E5.right")])]}),"instanceName":"1"});
            var Q14;
            Q14=makeQuery(id+"F15.opExtrude","SWEPT_BODY",BODY,{"disambiguationData":[OSD([sQuery(id+"F14.wireOp",EDGE,"E4.bottom"),sQuery(id+"F14.wireOp",EDGE,"E4.top"),sQuery(id+"F14.wireOp",EDGE,"E4.left"),sQuery(id+"F14.wireOp",EDGE,"E4.right")])]});
            var Q15;
            Q15=makeQuery(id+"F13.opPattern","COPY",BODY,{"derivedFrom":makeQuery(id+"F11.opPattern","COPY",BODY,{"derivedFrom":makeQuery(id+"F8.opExtrude","SWEPT_BODY",BODY,{"disambiguationData":[OSD([sQuery(id+"F7.wireOp",EDGE,"E3.bottom"),sQuery(id+"F7.wireOp",EDGE,"E3.top"),sQuery(id+"F7.wireOp",EDGE,"E3.left"),sQuery(id+"F7.wireOp",EDGE,"E3.right")])]}),"instanceName":"1"}),"instanceName":"1"});
            var Q16;
            Q16=makeQuery(id+"F11.opPattern","COPY",BODY,{"derivedFrom":makeQuery(id+"F8.opExtrude","SWEPT_BODY",BODY,{"disambiguationData":[OSD([sQuery(id+"F7.wireOp",EDGE,"E3.bottom"),sQuery(id+"F7.wireOp",EDGE,"E3.top"),sQuery(id+"F7.wireOp",EDGE,"E3.left"),sQuery(id+"F7.wireOp",EDGE,"E3.right")])]}),"instanceName":"1"});
            var Q17;
            Q17=makeQuery(id+"F20.opPattern","COPY",BODY,{"derivedFrom":makeQuery(id+"F15.opExtrude","SWEPT_BODY",BODY,{"disambiguationData":[OSD([sQuery(id+"F14.wireOp",EDGE,"E4.bottom"),sQuery(id+"F14.wireOp",EDGE,"E4.top"),sQuery(id+"F14.wireOp",EDGE,"E4.left"),sQuery(id+"F14.wireOp",EDGE,"E4.right")])]}),"instanceName":"1"});
            var Q18;
            Q18=makeQuery(id+"F13.opPattern","COPY",BODY,{"derivedFrom":makeQuery(id+"F10.opPattern","COPY",BODY,{"derivedFrom":makeQuery(id+"F8.opExtrude","SWEPT_BODY",BODY,{"disambiguationData":[OSD([sQuery(id+"F7.wireOp",EDGE,"E3.bottom"),sQuery(id+"F7.wireOp",EDGE,"E3.top"),sQuery(id+"F7.wireOp",EDGE,"E3.left"),sQuery(id+"F7.wireOp",EDGE,"E3.right")])]}),"instanceName":"1"}),"instanceName":"1"});
            var Q19;
            Q19=makeQuery(id+"F23.opExtrude","SWEPT_BODY",BODY,{"disambiguationData":[OSD([sQuery(id+"F22.wireOp",EDGE,"E5.bottom"),sQuery(id+"F22.wireOp",EDGE,"E5.top"),sQuery(id+"F22.wireOp",EDGE,"E5.left"),sQuery(id+"F22.wireOp",EDGE,"E5.right")])]});
            var Q20;
            Q20=makeQuery(id+"F10.opPattern","COPY",BODY,{"derivedFrom":makeQuery(id+"F8.opExtrude","SWEPT_BODY",BODY,{"disambiguationData":[OSD([sQuery(id+"F7.wireOp",EDGE,"E3.bottom"),sQuery(id+"F7.wireOp",EDGE,"E3.top"),sQuery(id+"F7.wireOp",EDGE,"E3.left"),sQuery(id+"F7.wireOp",EDGE,"E3.right")])]}),"instanceName":"1"});
            var Q21;
            Q21=makeQuery(id+"F27.opPattern","COPY",EDGE,{"derivedFrom":makeQuery(id+"F5.opExtrude","CAP_EDGE",EDGE,{"disambiguationData":[OSD([sQuery(id+"F4.wireOp",EDGE,"E2.top")])],"isStart":false}),"instanceName":"1"});
            transform(context, id + "F35", {"entities" : qUnion([Q0, Q1, Q2, Q3, Q4, Q5, Q6, Q7, Q8, Q9, Q10, Q11, Q12, Q13, Q14, Q15, Q16, Q17, Q18, Q19, Q20]), "transformType" : TransformType.ROTATION, "transformAxis" : qUnion([Q21]), "angle" : 90 * degree, "makeCopy" : true});
        }
        {
            var Q0;
            Q0=makeQuery(id+"F35.opPattern","COPY",EDGE,{"derivedFrom":makeQuery(id+"F5.opExtrude","CAP_EDGE",EDGE,{"disambiguationData":[OSD([sQuery(id+"F4.wireOp",EDGE,"E2.left")])],"isStart":true}),"instanceName":"1"});
            cPoint(context, id + "F36", {"entities" : qUnion([Q0]), "parameter" : 0.5});
        }
        {
            var Q0;
            Q0=makeQuery(id+"F35.opPattern","COPY",BODY,{"derivedFrom":makeQuery(id+"F31.opPattern","COPY",BODY,{"derivedFrom":makeQuery(id+"F2.opExtrude","SWEPT_BODY",BODY,{"disambiguationData":[OSD([sQuery(id+"F1.wireOp",EDGE,"E1.bottom"),sQuery(id+"F1.wireOp",EDGE,"E1.top"),sQuery(id+"F1.wireOp",EDGE,"E1.left"),sQuery(id+"F1.wireOp",EDGE,"E1.right")])]}),"instanceName":"1"}),"instanceName":"1"});
            var Q1;
            Q1=makeQuery(id+"F35.opPattern","COPY",BODY,{"derivedFrom":makeQuery(id+"F25.opPattern","COPY",BODY,{"derivedFrom":makeQuery(id+"F24.opPattern","COPY",BODY,{"derivedFrom":makeQuery(id+"F23.opExtrude","SWEPT_BODY",BODY,{"disambiguationData":[OSD([sQuery(id+"F22.wireOp",EDGE,"E5.bottom"),sQuery(id+"F22.wireOp",EDGE,"E5.top"),sQuery(id+"F22.wireOp",EDGE,"E5.left"),sQuery(id+"F22.wireOp",EDGE,"E5.right")])]}),"instanceName":"1"}),"instanceName":"1"}),"instanceName":"1"});
            var Q2;
            Q2=makeQuery(id+"F35.opPattern","COPY",BODY,{"derivedFrom":makeQuery(id+"F27.opPattern","COPY",BODY,{"derivedFrom":makeQuery(id+"F5.opExtrude","SWEPT_BODY",BODY,{"disambiguationData":[OSD([sQuery(id+"F4.wireOp",EDGE,"E2.bottom"),sQuery(id+"F4.wireOp",EDGE,"E2.top"),sQuery(id+"F4.wireOp",EDGE,"E2.left"),sQuery(id+"F4.wireOp",EDGE,"E2.right")])]}),"instanceName":"1"}),"instanceName":"1"});
            var Q3;
            Q3=makeQuery(id+"F35.opPattern","COPY",BODY,{"derivedFrom":makeQuery(id+"F2.opExtrude","SWEPT_BODY",BODY,{"disambiguationData":[OSD([sQuery(id+"F1.wireOp",EDGE,"E1.bottom"),sQuery(id+"F1.wireOp",EDGE,"E1.top"),sQuery(id+"F1.wireOp",EDGE,"E1.left"),sQuery(id+"F1.wireOp",EDGE,"E1.right")])]}),"instanceName":"1"});
            var Q4;
            Q4=makeQuery(id+"F35.opPattern","COPY",BODY,{"derivedFrom":makeQuery(id+"F13.opPattern","COPY",BODY,{"derivedFrom":makeQuery(id+"F8.opExtrude","SWEPT_BODY",BODY,{"disambiguationData":[OSD([sQuery(id+"F7.wireOp",EDGE,"E3.bottom"),sQuery(id+"F7.wireOp",EDGE,"E3.top"),sQuery(id+"F7.wireOp",EDGE,"E3.left"),sQuery(id+"F7.wireOp",EDGE,"E3.right")])]}),"instanceName":"1"}),"instanceName":"1"});
            var Q5;
            Q5=makeQuery(id+"F35.opPattern","COPY",BODY,{"derivedFrom":makeQuery(id+"F13.opPattern","COPY",BODY,{"derivedFrom":makeQuery(id+"F11.opPattern","COPY",BODY,{"derivedFrom":makeQuery(id+"F8.opExtrude","SWEPT_BODY",BODY,{"disambiguationData":[OSD([sQuery(id+"F7.wireOp",EDGE,"E3.bottom"),sQuery(id+"F7.wireOp",EDGE,"E3.top"),sQuery(id+"F7.wireOp",EDGE,"E3.left"),sQuery(id+"F7.wireOp",EDGE,"E3.right")])]}),"instanceName":"1"}),"instanceName":"1"}),"instanceName":"1"});
            var Q6;
            Q6=makeQuery(id+"F35.opPattern","COPY",BODY,{"derivedFrom":makeQuery(id+"F24.opPattern","COPY",BODY,{"derivedFrom":makeQuery(id+"F23.opExtrude","SWEPT_BODY",BODY,{"disambiguationData":[OSD([sQuery(id+"F22.wireOp",EDGE,"E5.bottom"),sQuery(id+"F22.wireOp",EDGE,"E5.top"),sQuery(id+"F22.wireOp",EDGE,"E5.left"),sQuery(id+"F22.wireOp",EDGE,"E5.right")])]}),"instanceName":"1"}),"instanceName":"1"});
            var Q7;
            Q7=makeQuery(id+"F35.opPattern","COPY",BODY,{"derivedFrom":makeQuery(id+"F13.opPattern","COPY",BODY,{"derivedFrom":makeQuery(id+"F10.opPattern","COPY",BODY,{"derivedFrom":makeQuery(id+"F8.opExtrude","SWEPT_BODY",BODY,{"disambiguationData":[OSD([sQuery(id+"F7.wireOp",EDGE,"E3.bottom"),sQuery(id+"F7.wireOp",EDGE,"E3.top"),sQuery(id+"F7.wireOp",EDGE,"E3.left"),sQuery(id+"F7.wireOp",EDGE,"E3.right")])]}),"instanceName":"1"}),"instanceName":"1"}),"instanceName":"1"});
            var Q8;
            Q8=makeQuery(id+"F35.opPattern","COPY",BODY,{"derivedFrom":makeQuery(id+"F23.opExtrude","SWEPT_BODY",BODY,{"disambiguationData":[OSD([sQuery(id+"F22.wireOp",EDGE,"E5.bottom"),sQuery(id+"F22.wireOp",EDGE,"E5.top"),sQuery(id+"F22.wireOp",EDGE,"E5.left"),sQuery(id+"F22.wireOp",EDGE,"E5.right")])]}),"instanceName":"1"});
            var Q9;
            Q9=makeQuery(id+"F35.opPattern","COPY",BODY,{"derivedFrom":makeQuery(id+"F29.opPattern","COPY",BODY,{"derivedFrom":makeQuery(id+"F27.opPattern","COPY",BODY,{"derivedFrom":makeQuery(id+"F5.opExtrude","SWEPT_BODY",BODY,{"disambiguationData":[OSD([sQuery(id+"F4.wireOp",EDGE,"E2.bottom"),sQuery(id+"F4.wireOp",EDGE,"E2.top"),sQuery(id+"F4.wireOp",EDGE,"E2.left"),sQuery(id+"F4.wireOp",EDGE,"E2.right")])]}),"instanceName":"1"}),"instanceName":"1"}),"instanceName":"1"});
            var Q10;
            Q10=makeQuery(id+"F35.opPattern","COPY",BODY,{"derivedFrom":makeQuery(id+"F30.opPattern","COPY",BODY,{"derivedFrom":makeQuery(id+"F29.opPattern","COPY",BODY,{"derivedFrom":makeQuery(id+"F27.opPattern","COPY",BODY,{"derivedFrom":makeQuery(id+"F5.opExtrude","SWEPT_BODY",BODY,{"disambiguationData":[OSD([sQuery(id+"F4.wireOp",EDGE,"E2.bottom"),sQuery(id+"F4.wireOp",EDGE,"E2.top"),sQuery(id+"F4.wireOp",EDGE,"E2.left"),sQuery(id+"F4.wireOp",EDGE,"E2.right")])]}),"instanceName":"1"}),"instanceName":"1"}),"instanceName":"1"}),"instanceName":"1"});
            var Q11;
            Q11=makeQuery(id+"F35.opPattern","COPY",BODY,{"derivedFrom":makeQuery(id+"F33.opPattern","COPY",BODY,{"derivedFrom":makeQuery(id+"F31.opPattern","COPY",BODY,{"derivedFrom":makeQuery(id+"F2.opExtrude","SWEPT_BODY",BODY,{"disambiguationData":[OSD([sQuery(id+"F1.wireOp",EDGE,"E1.bottom"),sQuery(id+"F1.wireOp",EDGE,"E1.top"),sQuery(id+"F1.wireOp",EDGE,"E1.left"),sQuery(id+"F1.wireOp",EDGE,"E1.right")])]}),"instanceName":"1"}),"instanceName":"1"}),"instanceName":"1"});
            var Q12;
            Q12=makeQuery(id+"F35.opPattern","COPY",BODY,{"derivedFrom":makeQuery(id+"F19.opPattern","COPY",BODY,{"derivedFrom":makeQuery(id+"F15.opExtrude","SWEPT_BODY",BODY,{"disambiguationData":[OSD([sQuery(id+"F14.wireOp",EDGE,"E4.bottom"),sQuery(id+"F14.wireOp",EDGE,"E4.top"),sQuery(id+"F14.wireOp",EDGE,"E4.left"),sQuery(id+"F14.wireOp",EDGE,"E4.right")])]}),"instanceName":"1"}),"instanceName":"1"});
            var Q13;
            Q13=makeQuery(id+"F35.opPattern","COPY",BODY,{"derivedFrom":makeQuery(id+"F8.opExtrude","SWEPT_BODY",BODY,{"disambiguationData":[OSD([sQuery(id+"F7.wireOp",EDGE,"E3.bottom"),sQuery(id+"F7.wireOp",EDGE,"E3.top"),sQuery(id+"F7.wireOp",EDGE,"E3.left"),sQuery(id+"F7.wireOp",EDGE,"E3.right")])]}),"instanceName":"1"});
            var Q14;
            Q14=makeQuery(id+"F35.opPattern","COPY",BODY,{"derivedFrom":makeQuery(id+"F5.opExtrude","SWEPT_BODY",BODY,{"disambiguationData":[OSD([sQuery(id+"F4.wireOp",EDGE,"E2.bottom"),sQuery(id+"F4.wireOp",EDGE,"E2.top"),sQuery(id+"F4.wireOp",EDGE,"E2.left"),sQuery(id+"F4.wireOp",EDGE,"E2.right")])]}),"instanceName":"1"});
            var Q15;
            Q15=makeQuery(id+"F35.opPattern","COPY",BODY,{"derivedFrom":makeQuery(id+"F3.opPattern","COPY",BODY,{"derivedFrom":makeQuery(id+"F2.opExtrude","SWEPT_BODY",BODY,{"disambiguationData":[OSD([sQuery(id+"F1.wireOp",EDGE,"E1.bottom"),sQuery(id+"F1.wireOp",EDGE,"E1.top"),sQuery(id+"F1.wireOp",EDGE,"E1.left"),sQuery(id+"F1.wireOp",EDGE,"E1.right")])]}),"instanceName":"1"}),"instanceName":"1"});
            var Q16;
            Q16=makeQuery(id+"F35.opPattern","COPY",BODY,{"derivedFrom":makeQuery(id+"F6.opPattern","COPY",BODY,{"derivedFrom":makeQuery(id+"F5.opExtrude","SWEPT_BODY",BODY,{"disambiguationData":[OSD([sQuery(id+"F4.wireOp",EDGE,"E2.bottom"),sQuery(id+"F4.wireOp",EDGE,"E2.top"),sQuery(id+"F4.wireOp",EDGE,"E2.left"),sQuery(id+"F4.wireOp",EDGE,"E2.right")])]}),"instanceName":"1"}),"instanceName":"1"});
            var Q17;
            Q17=makeQuery(id+"F35.opPattern","COPY",BODY,{"derivedFrom":makeQuery(id+"F15.opExtrude","SWEPT_BODY",BODY,{"disambiguationData":[OSD([sQuery(id+"F14.wireOp",EDGE,"E4.bottom"),sQuery(id+"F14.wireOp",EDGE,"E4.top"),sQuery(id+"F14.wireOp",EDGE,"E4.left"),sQuery(id+"F14.wireOp",EDGE,"E4.right")])]}),"instanceName":"1"});
            var Q18;
            Q18=makeQuery(id+"F35.opPattern","COPY",BODY,{"derivedFrom":makeQuery(id+"F11.opPattern","COPY",BODY,{"derivedFrom":makeQuery(id+"F8.opExtrude","SWEPT_BODY",BODY,{"disambiguationData":[OSD([sQuery(id+"F7.wireOp",EDGE,"E3.bottom"),sQuery(id+"F7.wireOp",EDGE,"E3.top"),sQuery(id+"F7.wireOp",EDGE,"E3.left"),sQuery(id+"F7.wireOp",EDGE,"E3.right")])]}),"instanceName":"1"}),"instanceName":"1"});
            var Q19;
            Q19=makeQuery(id+"F35.opPattern","COPY",BODY,{"derivedFrom":makeQuery(id+"F20.opPattern","COPY",BODY,{"derivedFrom":makeQuery(id+"F15.opExtrude","SWEPT_BODY",BODY,{"disambiguationData":[OSD([sQuery(id+"F14.wireOp",EDGE,"E4.bottom"),sQuery(id+"F14.wireOp",EDGE,"E4.top"),sQuery(id+"F14.wireOp",EDGE,"E4.left"),sQuery(id+"F14.wireOp",EDGE,"E4.right")])]}),"instanceName":"1"}),"instanceName":"1"});
            var Q20;
            Q20=makeQuery(id+"F35.opPattern","COPY",BODY,{"derivedFrom":makeQuery(id+"F10.opPattern","COPY",BODY,{"derivedFrom":makeQuery(id+"F8.opExtrude","SWEPT_BODY",BODY,{"disambiguationData":[OSD([sQuery(id+"F7.wireOp",EDGE,"E3.bottom"),sQuery(id+"F7.wireOp",EDGE,"E3.top"),sQuery(id+"F7.wireOp",EDGE,"E3.left"),sQuery(id+"F7.wireOp",EDGE,"E3.right")])]}),"instanceName":"1"}),"instanceName":"1"});
            var Q21;
            Q21=qCreatedBy(id+"F36",VERTEX);
            var Q22;
            Q22=makeQuery(id+"F35.opPattern","COPY",EDGE,{"derivedFrom":makeQuery(id+"F19.opPattern","COPY",EDGE,{"derivedFrom":makeQuery(id+"F15.opExtrude","CAP_EDGE",EDGE,{"disambiguationData":[OSD([sQuery(id+"F14.wireOp",EDGE,"E4.top")])],"isStart":false}),"instanceName":"1"}),"instanceName":"1"});
            transform(context, id + "F37", {"entities" : qUnion([Q0, Q1, Q2, Q3, Q4, Q5, Q6, Q7, Q8, Q9, Q10, Q11, Q12, Q13, Q14, Q15, Q16, Q17, Q18, Q19, Q20]), "transformType" : TransformType.TRANSLATION_DISTANCE, "transformDirection" : qUnion([Q21, Q22]), "distance" : 649 * mm, "oppositeDirection" : true, "makeCopy" : false});
        }
        {
            var Q0;
            Q0=makeQuery(id+"F2.opExtrude","SWEPT_BODY",BODY,{"disambiguationData":[OSD([sQuery(id+"F1.wireOp",EDGE,"E1.bottom"),sQuery(id+"F1.wireOp",EDGE,"E1.top"),sQuery(id+"F1.wireOp",EDGE,"E1.left"),sQuery(id+"F1.wireOp",EDGE,"E1.right")])]});
            var Q1;
            Q1=makeQuery(id+"F3.opPattern","COPY",BODY,{"derivedFrom":makeQuery(id+"F2.opExtrude","SWEPT_BODY",BODY,{"disambiguationData":[OSD([sQuery(id+"F1.wireOp",EDGE,"E1.bottom"),sQuery(id+"F1.wireOp",EDGE,"E1.top"),sQuery(id+"F1.wireOp",EDGE,"E1.left"),sQuery(id+"F1.wireOp",EDGE,"E1.right")])]}),"instanceName":"1"});
            var Q2;
            Q2=makeQuery(id+"F25.opPattern","COPY",BODY,{"derivedFrom":makeQuery(id+"F24.opPattern","COPY",BODY,{"derivedFrom":makeQuery(id+"F23.opExtrude","SWEPT_BODY",BODY,{"disambiguationData":[OSD([sQuery(id+"F22.wireOp",EDGE,"E5.bottom"),sQuery(id+"F22.wireOp",EDGE,"E5.top"),sQuery(id+"F22.wireOp",EDGE,"E5.left"),sQuery(id+"F22.wireOp",EDGE,"E5.right")])]}),"instanceName":"1"}),"instanceName":"1"});
            var Q3;
            Q3=makeQuery(id+"F13.opPattern","COPY",BODY,{"derivedFrom":makeQuery(id+"F8.opExtrude","SWEPT_BODY",BODY,{"disambiguationData":[OSD([sQuery(id+"F7.wireOp",EDGE,"E3.bottom"),sQuery(id+"F7.wireOp",EDGE,"E3.top"),sQuery(id+"F7.wireOp",EDGE,"E3.left"),sQuery(id+"F7.wireOp",EDGE,"E3.right")])]}),"instanceName":"1"});
            var Q4;
            Q4=makeQuery(id+"F27.opPattern","COPY",BODY,{"derivedFrom":makeQuery(id+"F5.opExtrude","SWEPT_BODY",BODY,{"disambiguationData":[OSD([sQuery(id+"F4.wireOp",EDGE,"E2.bottom"),sQuery(id+"F4.wireOp",EDGE,"E2.top"),sQuery(id+"F4.wireOp",EDGE,"E2.left"),sQuery(id+"F4.wireOp",EDGE,"E2.right")])]}),"instanceName":"1"});
            var Q5;
            Q5=makeQuery(id+"F8.opExtrude","SWEPT_BODY",BODY,{"disambiguationData":[OSD([sQuery(id+"F7.wireOp",EDGE,"E3.bottom"),sQuery(id+"F7.wireOp",EDGE,"E3.top"),sQuery(id+"F7.wireOp",EDGE,"E3.left"),sQuery(id+"F7.wireOp",EDGE,"E3.right")])]});
            var Q6;
            Q6=makeQuery(id+"F5.opExtrude","SWEPT_BODY",BODY,{"disambiguationData":[OSD([sQuery(id+"F4.wireOp",EDGE,"E2.bottom"),sQuery(id+"F4.wireOp",EDGE,"E2.top"),sQuery(id+"F4.wireOp",EDGE,"E2.left"),sQuery(id+"F4.wireOp",EDGE,"E2.right")])]});
            var Q7;
            Q7=makeQuery(id+"F31.opPattern","COPY",BODY,{"derivedFrom":makeQuery(id+"F2.opExtrude","SWEPT_BODY",BODY,{"disambiguationData":[OSD([sQuery(id+"F1.wireOp",EDGE,"E1.bottom"),sQuery(id+"F1.wireOp",EDGE,"E1.top"),sQuery(id+"F1.wireOp",EDGE,"E1.left"),sQuery(id+"F1.wireOp",EDGE,"E1.right")])]}),"instanceName":"1"});
            var Q8;
            Q8=makeQuery(id+"F29.opPattern","COPY",BODY,{"derivedFrom":makeQuery(id+"F27.opPattern","COPY",BODY,{"derivedFrom":makeQuery(id+"F5.opExtrude","SWEPT_BODY",BODY,{"disambiguationData":[OSD([sQuery(id+"F4.wireOp",EDGE,"E2.bottom"),sQuery(id+"F4.wireOp",EDGE,"E2.top"),sQuery(id+"F4.wireOp",EDGE,"E2.left"),sQuery(id+"F4.wireOp",EDGE,"E2.right")])]}),"instanceName":"1"}),"instanceName":"1"});
            var Q9;
            Q9=makeQuery(id+"F19.opPattern","COPY",BODY,{"derivedFrom":makeQuery(id+"F15.opExtrude","SWEPT_BODY",BODY,{"disambiguationData":[OSD([sQuery(id+"F14.wireOp",EDGE,"E4.bottom"),sQuery(id+"F14.wireOp",EDGE,"E4.top"),sQuery(id+"F14.wireOp",EDGE,"E4.left"),sQuery(id+"F14.wireOp",EDGE,"E4.right")])]}),"instanceName":"1"});
            var Q10;
            Q10=makeQuery(id+"F30.opPattern","COPY",BODY,{"derivedFrom":makeQuery(id+"F29.opPattern","COPY",BODY,{"derivedFrom":makeQuery(id+"F27.opPattern","COPY",BODY,{"derivedFrom":makeQuery(id+"F5.opExtrude","SWEPT_BODY",BODY,{"disambiguationData":[OSD([sQuery(id+"F4.wireOp",EDGE,"E2.bottom"),sQuery(id+"F4.wireOp",EDGE,"E2.top"),sQuery(id+"F4.wireOp",EDGE,"E2.left"),sQuery(id+"F4.wireOp",EDGE,"E2.right")])]}),"instanceName":"1"}),"instanceName":"1"}),"instanceName":"1"});
            var Q11;
            Q11=makeQuery(id+"F33.opPattern","COPY",BODY,{"derivedFrom":makeQuery(id+"F31.opPattern","COPY",BODY,{"derivedFrom":makeQuery(id+"F2.opExtrude","SWEPT_BODY",BODY,{"disambiguationData":[OSD([sQuery(id+"F1.wireOp",EDGE,"E1.bottom"),sQuery(id+"F1.wireOp",EDGE,"E1.top"),sQuery(id+"F1.wireOp",EDGE,"E1.left"),sQuery(id+"F1.wireOp",EDGE,"E1.right")])]}),"instanceName":"1"}),"instanceName":"1"});
            var Q12;
            Q12=makeQuery(id+"F6.opPattern","COPY",BODY,{"derivedFrom":makeQuery(id+"F5.opExtrude","SWEPT_BODY",BODY,{"disambiguationData":[OSD([sQuery(id+"F4.wireOp",EDGE,"E2.bottom"),sQuery(id+"F4.wireOp",EDGE,"E2.top"),sQuery(id+"F4.wireOp",EDGE,"E2.left"),sQuery(id+"F4.wireOp",EDGE,"E2.right")])]}),"instanceName":"1"});
            var Q13;
            Q13=makeQuery(id+"F15.opExtrude","SWEPT_BODY",BODY,{"disambiguationData":[OSD([sQuery(id+"F14.wireOp",EDGE,"E4.bottom"),sQuery(id+"F14.wireOp",EDGE,"E4.top"),sQuery(id+"F14.wireOp",EDGE,"E4.left"),sQuery(id+"F14.wireOp",EDGE,"E4.right")])]});
            var Q14;
            Q14=makeQuery(id+"F13.opPattern","COPY",BODY,{"derivedFrom":makeQuery(id+"F11.opPattern","COPY",BODY,{"derivedFrom":makeQuery(id+"F8.opExtrude","SWEPT_BODY",BODY,{"disambiguationData":[OSD([sQuery(id+"F7.wireOp",EDGE,"E3.bottom"),sQuery(id+"F7.wireOp",EDGE,"E3.top"),sQuery(id+"F7.wireOp",EDGE,"E3.left"),sQuery(id+"F7.wireOp",EDGE,"E3.right")])]}),"instanceName":"1"}),"instanceName":"1"});
            var Q15;
            Q15=makeQuery(id+"F11.opPattern","COPY",BODY,{"derivedFrom":makeQuery(id+"F8.opExtrude","SWEPT_BODY",BODY,{"disambiguationData":[OSD([sQuery(id+"F7.wireOp",EDGE,"E3.bottom"),sQuery(id+"F7.wireOp",EDGE,"E3.top"),sQuery(id+"F7.wireOp",EDGE,"E3.left"),sQuery(id+"F7.wireOp",EDGE,"E3.right")])]}),"instanceName":"1"});
            var Q16;
            Q16=makeQuery(id+"F24.opPattern","COPY",BODY,{"derivedFrom":makeQuery(id+"F23.opExtrude","SWEPT_BODY",BODY,{"disambiguationData":[OSD([sQuery(id+"F22.wireOp",EDGE,"E5.bottom"),sQuery(id+"F22.wireOp",EDGE,"E5.top"),sQuery(id+"F22.wireOp",EDGE,"E5.left"),sQuery(id+"F22.wireOp",EDGE,"E5.right")])]}),"instanceName":"1"});
            var Q17;
            Q17=makeQuery(id+"F20.opPattern","COPY",BODY,{"derivedFrom":makeQuery(id+"F15.opExtrude","SWEPT_BODY",BODY,{"disambiguationData":[OSD([sQuery(id+"F14.wireOp",EDGE,"E4.bottom"),sQuery(id+"F14.wireOp",EDGE,"E4.top"),sQuery(id+"F14.wireOp",EDGE,"E4.left"),sQuery(id+"F14.wireOp",EDGE,"E4.right")])]}),"instanceName":"1"});
            var Q18;
            Q18=makeQuery(id+"F13.opPattern","COPY",BODY,{"derivedFrom":makeQuery(id+"F10.opPattern","COPY",BODY,{"derivedFrom":makeQuery(id+"F8.opExtrude","SWEPT_BODY",BODY,{"disambiguationData":[OSD([sQuery(id+"F7.wireOp",EDGE,"E3.bottom"),sQuery(id+"F7.wireOp",EDGE,"E3.top"),sQuery(id+"F7.wireOp",EDGE,"E3.left"),sQuery(id+"F7.wireOp",EDGE,"E3.right")])]}),"instanceName":"1"}),"instanceName":"1"});
            var Q19;
            Q19=makeQuery(id+"F10.opPattern","COPY",BODY,{"derivedFrom":makeQuery(id+"F8.opExtrude","SWEPT_BODY",BODY,{"disambiguationData":[OSD([sQuery(id+"F7.wireOp",EDGE,"E3.bottom"),sQuery(id+"F7.wireOp",EDGE,"E3.top"),sQuery(id+"F7.wireOp",EDGE,"E3.left"),sQuery(id+"F7.wireOp",EDGE,"E3.right")])]}),"instanceName":"1"});
            var Q20;
            Q20=makeQuery(id+"F23.opExtrude","SWEPT_BODY",BODY,{"disambiguationData":[OSD([sQuery(id+"F22.wireOp",EDGE,"E5.bottom"),sQuery(id+"F22.wireOp",EDGE,"E5.top"),sQuery(id+"F22.wireOp",EDGE,"E5.left"),sQuery(id+"F22.wireOp",EDGE,"E5.right")])]});
            var Q21;
            Q21=makeQuery(id+"F8.opExtrude","CAP_EDGE",EDGE,{"disambiguationData":[OSD([sQuery(id+"F7.wireOp",EDGE,"E3.left")])],"isStart":false});
            transform(context, id + "F38", {"entities" : qUnion([Q0, Q1, Q2, Q3, Q4, Q5, Q6, Q7, Q8, Q9, Q10, Q11, Q12, Q13, Q14, Q15, Q16, Q17, Q18, Q19, Q20]), "transformType" : TransformType.TRANSLATION_DISTANCE, "transformDirection" : qUnion([Q21]), "distance" : 152 * mm, "makeCopy" : true});
        }
        {
            var Q0;
            Q0=makeQuery(id+"F2.opExtrude","SWEPT_BODY",BODY,{"disambiguationData":[OSD([sQuery(id+"F1.wireOp",EDGE,"E1.bottom"),sQuery(id+"F1.wireOp",EDGE,"E1.top"),sQuery(id+"F1.wireOp",EDGE,"E1.left"),sQuery(id+"F1.wireOp",EDGE,"E1.right")])]});
            var Q1;
            Q1=makeQuery(id+"F3.opPattern","COPY",BODY,{"derivedFrom":makeQuery(id+"F2.opExtrude","SWEPT_BODY",BODY,{"disambiguationData":[OSD([sQuery(id+"F1.wireOp",EDGE,"E1.bottom"),sQuery(id+"F1.wireOp",EDGE,"E1.top"),sQuery(id+"F1.wireOp",EDGE,"E1.left"),sQuery(id+"F1.wireOp",EDGE,"E1.right")])]}),"instanceName":"1"});
            var Q2;
            Q2=makeQuery(id+"F25.opPattern","COPY",BODY,{"derivedFrom":makeQuery(id+"F24.opPattern","COPY",BODY,{"derivedFrom":makeQuery(id+"F23.opExtrude","SWEPT_BODY",BODY,{"disambiguationData":[OSD([sQuery(id+"F22.wireOp",EDGE,"E5.bottom"),sQuery(id+"F22.wireOp",EDGE,"E5.top"),sQuery(id+"F22.wireOp",EDGE,"E5.left"),sQuery(id+"F22.wireOp",EDGE,"E5.right")])]}),"instanceName":"1"}),"instanceName":"1"});
            var Q3;
            Q3=makeQuery(id+"F13.opPattern","COPY",BODY,{"derivedFrom":makeQuery(id+"F8.opExtrude","SWEPT_BODY",BODY,{"disambiguationData":[OSD([sQuery(id+"F7.wireOp",EDGE,"E3.bottom"),sQuery(id+"F7.wireOp",EDGE,"E3.top"),sQuery(id+"F7.wireOp",EDGE,"E3.left"),sQuery(id+"F7.wireOp",EDGE,"E3.right")])]}),"instanceName":"1"});
            var Q4;
            Q4=makeQuery(id+"F27.opPattern","COPY",BODY,{"derivedFrom":makeQuery(id+"F5.opExtrude","SWEPT_BODY",BODY,{"disambiguationData":[OSD([sQuery(id+"F4.wireOp",EDGE,"E2.bottom"),sQuery(id+"F4.wireOp",EDGE,"E2.top"),sQuery(id+"F4.wireOp",EDGE,"E2.left"),sQuery(id+"F4.wireOp",EDGE,"E2.right")])]}),"instanceName":"1"});
            var Q5;
            Q5=makeQuery(id+"F8.opExtrude","SWEPT_BODY",BODY,{"disambiguationData":[OSD([sQuery(id+"F7.wireOp",EDGE,"E3.bottom"),sQuery(id+"F7.wireOp",EDGE,"E3.top"),sQuery(id+"F7.wireOp",EDGE,"E3.left"),sQuery(id+"F7.wireOp",EDGE,"E3.right")])]});
            var Q6;
            Q6=makeQuery(id+"F5.opExtrude","SWEPT_BODY",BODY,{"disambiguationData":[OSD([sQuery(id+"F4.wireOp",EDGE,"E2.bottom"),sQuery(id+"F4.wireOp",EDGE,"E2.top"),sQuery(id+"F4.wireOp",EDGE,"E2.left"),sQuery(id+"F4.wireOp",EDGE,"E2.right")])]});
            var Q7;
            Q7=makeQuery(id+"F31.opPattern","COPY",BODY,{"derivedFrom":makeQuery(id+"F2.opExtrude","SWEPT_BODY",BODY,{"disambiguationData":[OSD([sQuery(id+"F1.wireOp",EDGE,"E1.bottom"),sQuery(id+"F1.wireOp",EDGE,"E1.top"),sQuery(id+"F1.wireOp",EDGE,"E1.left"),sQuery(id+"F1.wireOp",EDGE,"E1.right")])]}),"instanceName":"1"});
            var Q8;
            Q8=makeQuery(id+"F29.opPattern","COPY",BODY,{"derivedFrom":makeQuery(id+"F27.opPattern","COPY",BODY,{"derivedFrom":makeQuery(id+"F5.opExtrude","SWEPT_BODY",BODY,{"disambiguationData":[OSD([sQuery(id+"F4.wireOp",EDGE,"E2.bottom"),sQuery(id+"F4.wireOp",EDGE,"E2.top"),sQuery(id+"F4.wireOp",EDGE,"E2.left"),sQuery(id+"F4.wireOp",EDGE,"E2.right")])]}),"instanceName":"1"}),"instanceName":"1"});
            var Q9;
            Q9=makeQuery(id+"F35.opPattern","COPY",BODY,{"derivedFrom":makeQuery(id+"F31.opPattern","COPY",BODY,{"derivedFrom":makeQuery(id+"F2.opExtrude","SWEPT_BODY",BODY,{"disambiguationData":[OSD([sQuery(id+"F1.wireOp",EDGE,"E1.bottom"),sQuery(id+"F1.wireOp",EDGE,"E1.top"),sQuery(id+"F1.wireOp",EDGE,"E1.left"),sQuery(id+"F1.wireOp",EDGE,"E1.right")])]}),"instanceName":"1"}),"instanceName":"1"});
            var Q10;
            Q10=makeQuery(id+"F35.opPattern","COPY",BODY,{"derivedFrom":makeQuery(id+"F25.opPattern","COPY",BODY,{"derivedFrom":makeQuery(id+"F24.opPattern","COPY",BODY,{"derivedFrom":makeQuery(id+"F23.opExtrude","SWEPT_BODY",BODY,{"disambiguationData":[OSD([sQuery(id+"F22.wireOp",EDGE,"E5.bottom"),sQuery(id+"F22.wireOp",EDGE,"E5.top"),sQuery(id+"F22.wireOp",EDGE,"E5.left"),sQuery(id+"F22.wireOp",EDGE,"E5.right")])]}),"instanceName":"1"}),"instanceName":"1"}),"instanceName":"1"});
            var Q11;
            Q11=makeQuery(id+"F19.opPattern","COPY",BODY,{"derivedFrom":makeQuery(id+"F15.opExtrude","SWEPT_BODY",BODY,{"disambiguationData":[OSD([sQuery(id+"F14.wireOp",EDGE,"E4.bottom"),sQuery(id+"F14.wireOp",EDGE,"E4.top"),sQuery(id+"F14.wireOp",EDGE,"E4.left"),sQuery(id+"F14.wireOp",EDGE,"E4.right")])]}),"instanceName":"1"});
            var Q12;
            Q12=makeQuery(id+"F30.opPattern","COPY",BODY,{"derivedFrom":makeQuery(id+"F29.opPattern","COPY",BODY,{"derivedFrom":makeQuery(id+"F27.opPattern","COPY",BODY,{"derivedFrom":makeQuery(id+"F5.opExtrude","SWEPT_BODY",BODY,{"disambiguationData":[OSD([sQuery(id+"F4.wireOp",EDGE,"E2.bottom"),sQuery(id+"F4.wireOp",EDGE,"E2.top"),sQuery(id+"F4.wireOp",EDGE,"E2.left"),sQuery(id+"F4.wireOp",EDGE,"E2.right")])]}),"instanceName":"1"}),"instanceName":"1"}),"instanceName":"1"});
            var Q13;
            Q13=makeQuery(id+"F6.opPattern","COPY",BODY,{"derivedFrom":makeQuery(id+"F5.opExtrude","SWEPT_BODY",BODY,{"disambiguationData":[OSD([sQuery(id+"F4.wireOp",EDGE,"E2.bottom"),sQuery(id+"F4.wireOp",EDGE,"E2.top"),sQuery(id+"F4.wireOp",EDGE,"E2.left"),sQuery(id+"F4.wireOp",EDGE,"E2.right")])]}),"instanceName":"1"});
            var Q14;
            Q14=makeQuery(id+"F35.opPattern","COPY",BODY,{"derivedFrom":makeQuery(id+"F27.opPattern","COPY",BODY,{"derivedFrom":makeQuery(id+"F5.opExtrude","SWEPT_BODY",BODY,{"disambiguationData":[OSD([sQuery(id+"F4.wireOp",EDGE,"E2.bottom"),sQuery(id+"F4.wireOp",EDGE,"E2.top"),sQuery(id+"F4.wireOp",EDGE,"E2.left"),sQuery(id+"F4.wireOp",EDGE,"E2.right")])]}),"instanceName":"1"}),"instanceName":"1"});
            var Q15;
            Q15=makeQuery(id+"F35.opPattern","COPY",BODY,{"derivedFrom":makeQuery(id+"F29.opPattern","COPY",BODY,{"derivedFrom":makeQuery(id+"F27.opPattern","COPY",BODY,{"derivedFrom":makeQuery(id+"F5.opExtrude","SWEPT_BODY",BODY,{"disambiguationData":[OSD([sQuery(id+"F4.wireOp",EDGE,"E2.bottom"),sQuery(id+"F4.wireOp",EDGE,"E2.top"),sQuery(id+"F4.wireOp",EDGE,"E2.left"),sQuery(id+"F4.wireOp",EDGE,"E2.right")])]}),"instanceName":"1"}),"instanceName":"1"}),"instanceName":"1"});
            var Q16;
            Q16=makeQuery(id+"F35.opPattern","COPY",BODY,{"derivedFrom":makeQuery(id+"F30.opPattern","COPY",BODY,{"derivedFrom":makeQuery(id+"F29.opPattern","COPY",BODY,{"derivedFrom":makeQuery(id+"F27.opPattern","COPY",BODY,{"derivedFrom":makeQuery(id+"F5.opExtrude","SWEPT_BODY",BODY,{"disambiguationData":[OSD([sQuery(id+"F4.wireOp",EDGE,"E2.bottom"),sQuery(id+"F4.wireOp",EDGE,"E2.top"),sQuery(id+"F4.wireOp",EDGE,"E2.left"),sQuery(id+"F4.wireOp",EDGE,"E2.right")])]}),"instanceName":"1"}),"instanceName":"1"}),"instanceName":"1"}),"instanceName":"1"});
            var Q17;
            Q17=makeQuery(id+"F33.opPattern","COPY",BODY,{"derivedFrom":makeQuery(id+"F31.opPattern","COPY",BODY,{"derivedFrom":makeQuery(id+"F2.opExtrude","SWEPT_BODY",BODY,{"disambiguationData":[OSD([sQuery(id+"F1.wireOp",EDGE,"E1.bottom"),sQuery(id+"F1.wireOp",EDGE,"E1.top"),sQuery(id+"F1.wireOp",EDGE,"E1.left"),sQuery(id+"F1.wireOp",EDGE,"E1.right")])]}),"instanceName":"1"}),"instanceName":"1"});
            var Q18;
            Q18=makeQuery(id+"F35.opPattern","COPY",BODY,{"derivedFrom":makeQuery(id+"F33.opPattern","COPY",BODY,{"derivedFrom":makeQuery(id+"F31.opPattern","COPY",BODY,{"derivedFrom":makeQuery(id+"F2.opExtrude","SWEPT_BODY",BODY,{"disambiguationData":[OSD([sQuery(id+"F1.wireOp",EDGE,"E1.bottom"),sQuery(id+"F1.wireOp",EDGE,"E1.top"),sQuery(id+"F1.wireOp",EDGE,"E1.left"),sQuery(id+"F1.wireOp",EDGE,"E1.right")])]}),"instanceName":"1"}),"instanceName":"1"}),"instanceName":"1"});
            var Q19;
            Q19=makeQuery(id+"F35.opPattern","COPY",BODY,{"derivedFrom":makeQuery(id+"F24.opPattern","COPY",BODY,{"derivedFrom":makeQuery(id+"F23.opExtrude","SWEPT_BODY",BODY,{"disambiguationData":[OSD([sQuery(id+"F22.wireOp",EDGE,"E5.bottom"),sQuery(id+"F22.wireOp",EDGE,"E5.top"),sQuery(id+"F22.wireOp",EDGE,"E5.left"),sQuery(id+"F22.wireOp",EDGE,"E5.right")])]}),"instanceName":"1"}),"instanceName":"1"});
            var Q20;
            Q20=makeQuery(id+"F35.opPattern","COPY",BODY,{"derivedFrom":makeQuery(id+"F23.opExtrude","SWEPT_BODY",BODY,{"disambiguationData":[OSD([sQuery(id+"F22.wireOp",EDGE,"E5.bottom"),sQuery(id+"F22.wireOp",EDGE,"E5.top"),sQuery(id+"F22.wireOp",EDGE,"E5.left"),sQuery(id+"F22.wireOp",EDGE,"E5.right")])]}),"instanceName":"1"});
            var Q21;
            Q21=makeQuery(id+"F35.opPattern","COPY",BODY,{"derivedFrom":makeQuery(id+"F20.opPattern","COPY",BODY,{"derivedFrom":makeQuery(id+"F15.opExtrude","SWEPT_BODY",BODY,{"disambiguationData":[OSD([sQuery(id+"F14.wireOp",EDGE,"E4.bottom"),sQuery(id+"F14.wireOp",EDGE,"E4.top"),sQuery(id+"F14.wireOp",EDGE,"E4.left"),sQuery(id+"F14.wireOp",EDGE,"E4.right")])]}),"instanceName":"1"}),"instanceName":"1"});
            var Q22;
            Q22=makeQuery(id+"F35.opPattern","COPY",BODY,{"derivedFrom":makeQuery(id+"F19.opPattern","COPY",BODY,{"derivedFrom":makeQuery(id+"F15.opExtrude","SWEPT_BODY",BODY,{"disambiguationData":[OSD([sQuery(id+"F14.wireOp",EDGE,"E4.bottom"),sQuery(id+"F14.wireOp",EDGE,"E4.top"),sQuery(id+"F14.wireOp",EDGE,"E4.left"),sQuery(id+"F14.wireOp",EDGE,"E4.right")])]}),"instanceName":"1"}),"instanceName":"1"});
            var Q23;
            Q23=makeQuery(id+"F35.opPattern","COPY",BODY,{"derivedFrom":makeQuery(id+"F15.opExtrude","SWEPT_BODY",BODY,{"disambiguationData":[OSD([sQuery(id+"F14.wireOp",EDGE,"E4.bottom"),sQuery(id+"F14.wireOp",EDGE,"E4.top"),sQuery(id+"F14.wireOp",EDGE,"E4.left"),sQuery(id+"F14.wireOp",EDGE,"E4.right")])]}),"instanceName":"1"});
            var Q24;
            Q24=makeQuery(id+"F35.opPattern","COPY",BODY,{"derivedFrom":makeQuery(id+"F13.opPattern","COPY",BODY,{"derivedFrom":makeQuery(id+"F11.opPattern","COPY",BODY,{"derivedFrom":makeQuery(id+"F8.opExtrude","SWEPT_BODY",BODY,{"disambiguationData":[OSD([sQuery(id+"F7.wireOp",EDGE,"E3.bottom"),sQuery(id+"F7.wireOp",EDGE,"E3.top"),sQuery(id+"F7.wireOp",EDGE,"E3.left"),sQuery(id+"F7.wireOp",EDGE,"E3.right")])]}),"instanceName":"1"}),"instanceName":"1"}),"instanceName":"1"});
            var Q25;
            Q25=makeQuery(id+"F35.opPattern","COPY",BODY,{"derivedFrom":makeQuery(id+"F6.opPattern","COPY",BODY,{"derivedFrom":makeQuery(id+"F5.opExtrude","SWEPT_BODY",BODY,{"disambiguationData":[OSD([sQuery(id+"F4.wireOp",EDGE,"E2.bottom"),sQuery(id+"F4.wireOp",EDGE,"E2.top"),sQuery(id+"F4.wireOp",EDGE,"E2.left"),sQuery(id+"F4.wireOp",EDGE,"E2.right")])]}),"instanceName":"1"}),"instanceName":"1"});
            var Q26;
            Q26=makeQuery(id+"F35.opPattern","COPY",BODY,{"derivedFrom":makeQuery(id+"F8.opExtrude","SWEPT_BODY",BODY,{"disambiguationData":[OSD([sQuery(id+"F7.wireOp",EDGE,"E3.bottom"),sQuery(id+"F7.wireOp",EDGE,"E3.top"),sQuery(id+"F7.wireOp",EDGE,"E3.left"),sQuery(id+"F7.wireOp",EDGE,"E3.right")])]}),"instanceName":"1"});
            var Q27;
            Q27=makeQuery(id+"F35.opPattern","COPY",BODY,{"derivedFrom":makeQuery(id+"F5.opExtrude","SWEPT_BODY",BODY,{"disambiguationData":[OSD([sQuery(id+"F4.wireOp",EDGE,"E2.bottom"),sQuery(id+"F4.wireOp",EDGE,"E2.top"),sQuery(id+"F4.wireOp",EDGE,"E2.left"),sQuery(id+"F4.wireOp",EDGE,"E2.right")])]}),"instanceName":"1"});
            var Q28;
            Q28=makeQuery(id+"F35.opPattern","COPY",BODY,{"derivedFrom":makeQuery(id+"F3.opPattern","COPY",BODY,{"derivedFrom":makeQuery(id+"F2.opExtrude","SWEPT_BODY",BODY,{"disambiguationData":[OSD([sQuery(id+"F1.wireOp",EDGE,"E1.bottom"),sQuery(id+"F1.wireOp",EDGE,"E1.top"),sQuery(id+"F1.wireOp",EDGE,"E1.left"),sQuery(id+"F1.wireOp",EDGE,"E1.right")])]}),"instanceName":"1"}),"instanceName":"1"});
            var Q29;
            Q29=makeQuery(id+"F38.opPattern","COPY",BODY,{"derivedFrom":makeQuery(id+"F5.opExtrude","SWEPT_BODY",BODY,{"disambiguationData":[OSD([sQuery(id+"F4.wireOp",EDGE,"E2.bottom"),sQuery(id+"F4.wireOp",EDGE,"E2.top"),sQuery(id+"F4.wireOp",EDGE,"E2.left"),sQuery(id+"F4.wireOp",EDGE,"E2.right")])]}),"instanceName":"1"});
            var Q30;
            Q30=makeQuery(id+"F35.opPattern","COPY",BODY,{"derivedFrom":makeQuery(id+"F2.opExtrude","SWEPT_BODY",BODY,{"disambiguationData":[OSD([sQuery(id+"F1.wireOp",EDGE,"E1.bottom"),sQuery(id+"F1.wireOp",EDGE,"E1.top"),sQuery(id+"F1.wireOp",EDGE,"E1.left"),sQuery(id+"F1.wireOp",EDGE,"E1.right")])]}),"instanceName":"1"});
            var Q31;
            Q31=makeQuery(id+"F35.opPattern","COPY",BODY,{"derivedFrom":makeQuery(id+"F10.opPattern","COPY",BODY,{"derivedFrom":makeQuery(id+"F8.opExtrude","SWEPT_BODY",BODY,{"disambiguationData":[OSD([sQuery(id+"F7.wireOp",EDGE,"E3.bottom"),sQuery(id+"F7.wireOp",EDGE,"E3.top"),sQuery(id+"F7.wireOp",EDGE,"E3.left"),sQuery(id+"F7.wireOp",EDGE,"E3.right")])]}),"instanceName":"1"}),"instanceName":"1"});
            var Q32;
            Q32=makeQuery(id+"F35.opPattern","COPY",BODY,{"derivedFrom":makeQuery(id+"F11.opPattern","COPY",BODY,{"derivedFrom":makeQuery(id+"F8.opExtrude","SWEPT_BODY",BODY,{"disambiguationData":[OSD([sQuery(id+"F7.wireOp",EDGE,"E3.bottom"),sQuery(id+"F7.wireOp",EDGE,"E3.top"),sQuery(id+"F7.wireOp",EDGE,"E3.left"),sQuery(id+"F7.wireOp",EDGE,"E3.right")])]}),"instanceName":"1"}),"instanceName":"1"});
            var Q33;
            Q33=makeQuery(id+"F35.opPattern","COPY",BODY,{"derivedFrom":makeQuery(id+"F13.opPattern","COPY",BODY,{"derivedFrom":makeQuery(id+"F8.opExtrude","SWEPT_BODY",BODY,{"disambiguationData":[OSD([sQuery(id+"F7.wireOp",EDGE,"E3.bottom"),sQuery(id+"F7.wireOp",EDGE,"E3.top"),sQuery(id+"F7.wireOp",EDGE,"E3.left"),sQuery(id+"F7.wireOp",EDGE,"E3.right")])]}),"instanceName":"1"}),"instanceName":"1"});
            var Q34;
            Q34=makeQuery(id+"F35.opPattern","COPY",BODY,{"derivedFrom":makeQuery(id+"F13.opPattern","COPY",BODY,{"derivedFrom":makeQuery(id+"F10.opPattern","COPY",BODY,{"derivedFrom":makeQuery(id+"F8.opExtrude","SWEPT_BODY",BODY,{"disambiguationData":[OSD([sQuery(id+"F7.wireOp",EDGE,"E3.bottom"),sQuery(id+"F7.wireOp",EDGE,"E3.top"),sQuery(id+"F7.wireOp",EDGE,"E3.left"),sQuery(id+"F7.wireOp",EDGE,"E3.right")])]}),"instanceName":"1"}),"instanceName":"1"}),"instanceName":"1"});
            var Q35;
            Q35=makeQuery(id+"F38.opPattern","COPY",BODY,{"derivedFrom":makeQuery(id+"F6.opPattern","COPY",BODY,{"derivedFrom":makeQuery(id+"F5.opExtrude","SWEPT_BODY",BODY,{"disambiguationData":[OSD([sQuery(id+"F4.wireOp",EDGE,"E2.bottom"),sQuery(id+"F4.wireOp",EDGE,"E2.top"),sQuery(id+"F4.wireOp",EDGE,"E2.left"),sQuery(id+"F4.wireOp",EDGE,"E2.right")])]}),"instanceName":"1"}),"instanceName":"1"});
            var Q36;
            Q36=makeQuery(id+"F38.opPattern","COPY",BODY,{"derivedFrom":makeQuery(id+"F2.opExtrude","SWEPT_BODY",BODY,{"disambiguationData":[OSD([sQuery(id+"F1.wireOp",EDGE,"E1.bottom"),sQuery(id+"F1.wireOp",EDGE,"E1.top"),sQuery(id+"F1.wireOp",EDGE,"E1.left"),sQuery(id+"F1.wireOp",EDGE,"E1.right")])]}),"instanceName":"1"});
            var Q37;
            Q37=makeQuery(id+"F38.opPattern","COPY",BODY,{"derivedFrom":makeQuery(id+"F3.opPattern","COPY",BODY,{"derivedFrom":makeQuery(id+"F2.opExtrude","SWEPT_BODY",BODY,{"disambiguationData":[OSD([sQuery(id+"F1.wireOp",EDGE,"E1.bottom"),sQuery(id+"F1.wireOp",EDGE,"E1.top"),sQuery(id+"F1.wireOp",EDGE,"E1.left"),sQuery(id+"F1.wireOp",EDGE,"E1.right")])]}),"instanceName":"1"}),"instanceName":"1"});
            var Q38;
            Q38=makeQuery(id+"F38.opPattern","COPY",BODY,{"derivedFrom":makeQuery(id+"F8.opExtrude","SWEPT_BODY",BODY,{"disambiguationData":[OSD([sQuery(id+"F7.wireOp",EDGE,"E3.bottom"),sQuery(id+"F7.wireOp",EDGE,"E3.top"),sQuery(id+"F7.wireOp",EDGE,"E3.left"),sQuery(id+"F7.wireOp",EDGE,"E3.right")])]}),"instanceName":"1"});
            var Q39;
            Q39=makeQuery(id+"F38.opPattern","COPY",BODY,{"derivedFrom":makeQuery(id+"F10.opPattern","COPY",BODY,{"derivedFrom":makeQuery(id+"F8.opExtrude","SWEPT_BODY",BODY,{"disambiguationData":[OSD([sQuery(id+"F7.wireOp",EDGE,"E3.bottom"),sQuery(id+"F7.wireOp",EDGE,"E3.top"),sQuery(id+"F7.wireOp",EDGE,"E3.left"),sQuery(id+"F7.wireOp",EDGE,"E3.right")])]}),"instanceName":"1"}),"instanceName":"1"});
            var Q40;
            Q40=makeQuery(id+"F38.opPattern","COPY",BODY,{"derivedFrom":makeQuery(id+"F13.opPattern","COPY",BODY,{"derivedFrom":makeQuery(id+"F8.opExtrude","SWEPT_BODY",BODY,{"disambiguationData":[OSD([sQuery(id+"F7.wireOp",EDGE,"E3.bottom"),sQuery(id+"F7.wireOp",EDGE,"E3.top"),sQuery(id+"F7.wireOp",EDGE,"E3.left"),sQuery(id+"F7.wireOp",EDGE,"E3.right")])]}),"instanceName":"1"}),"instanceName":"1"});
            var Q41;
            Q41=makeQuery(id+"F38.opPattern","COPY",BODY,{"derivedFrom":makeQuery(id+"F19.opPattern","COPY",BODY,{"derivedFrom":makeQuery(id+"F15.opExtrude","SWEPT_BODY",BODY,{"disambiguationData":[OSD([sQuery(id+"F14.wireOp",EDGE,"E4.bottom"),sQuery(id+"F14.wireOp",EDGE,"E4.top"),sQuery(id+"F14.wireOp",EDGE,"E4.left"),sQuery(id+"F14.wireOp",EDGE,"E4.right")])]}),"instanceName":"1"}),"instanceName":"1"});
            var Q42;
            Q42=makeQuery(id+"F38.opPattern","COPY",BODY,{"derivedFrom":makeQuery(id+"F23.opExtrude","SWEPT_BODY",BODY,{"disambiguationData":[OSD([sQuery(id+"F22.wireOp",EDGE,"E5.bottom"),sQuery(id+"F22.wireOp",EDGE,"E5.top"),sQuery(id+"F22.wireOp",EDGE,"E5.left"),sQuery(id+"F22.wireOp",EDGE,"E5.right")])]}),"instanceName":"1"});
            var Q43;
            Q43=makeQuery(id+"F38.opPattern","COPY",BODY,{"derivedFrom":makeQuery(id+"F24.opPattern","COPY",BODY,{"derivedFrom":makeQuery(id+"F23.opExtrude","SWEPT_BODY",BODY,{"disambiguationData":[OSD([sQuery(id+"F22.wireOp",EDGE,"E5.bottom"),sQuery(id+"F22.wireOp",EDGE,"E5.top"),sQuery(id+"F22.wireOp",EDGE,"E5.left"),sQuery(id+"F22.wireOp",EDGE,"E5.right")])]}),"instanceName":"1"}),"instanceName":"1"});
            var Q44;
            Q44=makeQuery(id+"F38.opPattern","COPY",BODY,{"derivedFrom":makeQuery(id+"F25.opPattern","COPY",BODY,{"derivedFrom":makeQuery(id+"F24.opPattern","COPY",BODY,{"derivedFrom":makeQuery(id+"F23.opExtrude","SWEPT_BODY",BODY,{"disambiguationData":[OSD([sQuery(id+"F22.wireOp",EDGE,"E5.bottom"),sQuery(id+"F22.wireOp",EDGE,"E5.top"),sQuery(id+"F22.wireOp",EDGE,"E5.left"),sQuery(id+"F22.wireOp",EDGE,"E5.right")])]}),"instanceName":"1"}),"instanceName":"1"}),"instanceName":"1"});
            var Q45;
            Q45=makeQuery(id+"F38.opPattern","COPY",BODY,{"derivedFrom":makeQuery(id+"F27.opPattern","COPY",BODY,{"derivedFrom":makeQuery(id+"F5.opExtrude","SWEPT_BODY",BODY,{"disambiguationData":[OSD([sQuery(id+"F4.wireOp",EDGE,"E2.bottom"),sQuery(id+"F4.wireOp",EDGE,"E2.top"),sQuery(id+"F4.wireOp",EDGE,"E2.left"),sQuery(id+"F4.wireOp",EDGE,"E2.right")])]}),"instanceName":"1"}),"instanceName":"1"});
            var Q46;
            Q46=makeQuery(id+"F38.opPattern","COPY",BODY,{"derivedFrom":makeQuery(id+"F29.opPattern","COPY",BODY,{"derivedFrom":makeQuery(id+"F27.opPattern","COPY",BODY,{"derivedFrom":makeQuery(id+"F5.opExtrude","SWEPT_BODY",BODY,{"disambiguationData":[OSD([sQuery(id+"F4.wireOp",EDGE,"E2.bottom"),sQuery(id+"F4.wireOp",EDGE,"E2.top"),sQuery(id+"F4.wireOp",EDGE,"E2.left"),sQuery(id+"F4.wireOp",EDGE,"E2.right")])]}),"instanceName":"1"}),"instanceName":"1"}),"instanceName":"1"});
            var Q47;
            Q47=makeQuery(id+"F38.opPattern","COPY",BODY,{"derivedFrom":makeQuery(id+"F30.opPattern","COPY",BODY,{"derivedFrom":makeQuery(id+"F29.opPattern","COPY",BODY,{"derivedFrom":makeQuery(id+"F27.opPattern","COPY",BODY,{"derivedFrom":makeQuery(id+"F5.opExtrude","SWEPT_BODY",BODY,{"disambiguationData":[OSD([sQuery(id+"F4.wireOp",EDGE,"E2.bottom"),sQuery(id+"F4.wireOp",EDGE,"E2.top"),sQuery(id+"F4.wireOp",EDGE,"E2.left"),sQuery(id+"F4.wireOp",EDGE,"E2.right")])]}),"instanceName":"1"}),"instanceName":"1"}),"instanceName":"1"}),"instanceName":"1"});
            var Q48;
            Q48=makeQuery(id+"F38.opPattern","COPY",BODY,{"derivedFrom":makeQuery(id+"F31.opPattern","COPY",BODY,{"derivedFrom":makeQuery(id+"F2.opExtrude","SWEPT_BODY",BODY,{"disambiguationData":[OSD([sQuery(id+"F1.wireOp",EDGE,"E1.bottom"),sQuery(id+"F1.wireOp",EDGE,"E1.top"),sQuery(id+"F1.wireOp",EDGE,"E1.left"),sQuery(id+"F1.wireOp",EDGE,"E1.right")])]}),"instanceName":"1"}),"instanceName":"1"});
            var Q49;
            Q49=makeQuery(id+"F38.opPattern","COPY",BODY,{"derivedFrom":makeQuery(id+"F33.opPattern","COPY",BODY,{"derivedFrom":makeQuery(id+"F31.opPattern","COPY",BODY,{"derivedFrom":makeQuery(id+"F2.opExtrude","SWEPT_BODY",BODY,{"disambiguationData":[OSD([sQuery(id+"F1.wireOp",EDGE,"E1.bottom"),sQuery(id+"F1.wireOp",EDGE,"E1.top"),sQuery(id+"F1.wireOp",EDGE,"E1.left"),sQuery(id+"F1.wireOp",EDGE,"E1.right")])]}),"instanceName":"1"}),"instanceName":"1"}),"instanceName":"1"});
            var Q50;
            Q50=makeQuery(id+"F24.opPattern","COPY",BODY,{"derivedFrom":makeQuery(id+"F23.opExtrude","SWEPT_BODY",BODY,{"disambiguationData":[OSD([sQuery(id+"F22.wireOp",EDGE,"E5.bottom"),sQuery(id+"F22.wireOp",EDGE,"E5.top"),sQuery(id+"F22.wireOp",EDGE,"E5.left"),sQuery(id+"F22.wireOp",EDGE,"E5.right")])]}),"instanceName":"1"});
            var Q51;
            Q51=makeQuery(id+"F13.opPattern","COPY",BODY,{"derivedFrom":makeQuery(id+"F10.opPattern","COPY",BODY,{"derivedFrom":makeQuery(id+"F8.opExtrude","SWEPT_BODY",BODY,{"disambiguationData":[OSD([sQuery(id+"F7.wireOp",EDGE,"E3.bottom"),sQuery(id+"F7.wireOp",EDGE,"E3.top"),sQuery(id+"F7.wireOp",EDGE,"E3.left"),sQuery(id+"F7.wireOp",EDGE,"E3.right")])]}),"instanceName":"1"}),"instanceName":"1"});
            var Q52;
            Q52=makeQuery(id+"F23.opExtrude","SWEPT_BODY",BODY,{"disambiguationData":[OSD([sQuery(id+"F22.wireOp",EDGE,"E5.bottom"),sQuery(id+"F22.wireOp",EDGE,"E5.top"),sQuery(id+"F22.wireOp",EDGE,"E5.left"),sQuery(id+"F22.wireOp",EDGE,"E5.right")])]});
            var Q53;
            Q53=makeQuery(id+"F13.opPattern","COPY",BODY,{"derivedFrom":makeQuery(id+"F11.opPattern","COPY",BODY,{"derivedFrom":makeQuery(id+"F8.opExtrude","SWEPT_BODY",BODY,{"disambiguationData":[OSD([sQuery(id+"F7.wireOp",EDGE,"E3.bottom"),sQuery(id+"F7.wireOp",EDGE,"E3.top"),sQuery(id+"F7.wireOp",EDGE,"E3.left"),sQuery(id+"F7.wireOp",EDGE,"E3.right")])]}),"instanceName":"1"}),"instanceName":"1"});
            var Q54;
            Q54=makeQuery(id+"F11.opPattern","COPY",BODY,{"derivedFrom":makeQuery(id+"F8.opExtrude","SWEPT_BODY",BODY,{"disambiguationData":[OSD([sQuery(id+"F7.wireOp",EDGE,"E3.bottom"),sQuery(id+"F7.wireOp",EDGE,"E3.top"),sQuery(id+"F7.wireOp",EDGE,"E3.left"),sQuery(id+"F7.wireOp",EDGE,"E3.right")])]}),"instanceName":"1"});
            var Q55;
            Q55=makeQuery(id+"F10.opPattern","COPY",BODY,{"derivedFrom":makeQuery(id+"F8.opExtrude","SWEPT_BODY",BODY,{"disambiguationData":[OSD([sQuery(id+"F7.wireOp",EDGE,"E3.bottom"),sQuery(id+"F7.wireOp",EDGE,"E3.top"),sQuery(id+"F7.wireOp",EDGE,"E3.left"),sQuery(id+"F7.wireOp",EDGE,"E3.right")])]}),"instanceName":"1"});
            var Q56;
            Q56=makeQuery(id+"F38.opPattern","COPY",BODY,{"derivedFrom":makeQuery(id+"F11.opPattern","COPY",BODY,{"derivedFrom":makeQuery(id+"F8.opExtrude","SWEPT_BODY",BODY,{"disambiguationData":[OSD([sQuery(id+"F7.wireOp",EDGE,"E3.bottom"),sQuery(id+"F7.wireOp",EDGE,"E3.top"),sQuery(id+"F7.wireOp",EDGE,"E3.left"),sQuery(id+"F7.wireOp",EDGE,"E3.right")])]}),"instanceName":"1"}),"instanceName":"1"});
            var Q57;
            Q57=makeQuery(id+"F38.opPattern","COPY",BODY,{"derivedFrom":makeQuery(id+"F13.opPattern","COPY",BODY,{"derivedFrom":makeQuery(id+"F10.opPattern","COPY",BODY,{"derivedFrom":makeQuery(id+"F8.opExtrude","SWEPT_BODY",BODY,{"disambiguationData":[OSD([sQuery(id+"F7.wireOp",EDGE,"E3.bottom"),sQuery(id+"F7.wireOp",EDGE,"E3.top"),sQuery(id+"F7.wireOp",EDGE,"E3.left"),sQuery(id+"F7.wireOp",EDGE,"E3.right")])]}),"instanceName":"1"}),"instanceName":"1"}),"instanceName":"1"});
            var Q58;
            Q58=makeQuery(id+"F38.opPattern","COPY",BODY,{"derivedFrom":makeQuery(id+"F15.opExtrude","SWEPT_BODY",BODY,{"disambiguationData":[OSD([sQuery(id+"F14.wireOp",EDGE,"E4.bottom"),sQuery(id+"F14.wireOp",EDGE,"E4.top"),sQuery(id+"F14.wireOp",EDGE,"E4.left"),sQuery(id+"F14.wireOp",EDGE,"E4.right")])]}),"instanceName":"1"});
            var Q59;
            Q59=makeQuery(id+"F20.opPattern","COPY",BODY,{"derivedFrom":makeQuery(id+"F15.opExtrude","SWEPT_BODY",BODY,{"disambiguationData":[OSD([sQuery(id+"F14.wireOp",EDGE,"E4.bottom"),sQuery(id+"F14.wireOp",EDGE,"E4.top"),sQuery(id+"F14.wireOp",EDGE,"E4.left"),sQuery(id+"F14.wireOp",EDGE,"E4.right")])]}),"instanceName":"1"});
            var Q60;
            Q60=makeQuery(id+"F15.opExtrude","SWEPT_BODY",BODY,{"disambiguationData":[OSD([sQuery(id+"F14.wireOp",EDGE,"E4.bottom"),sQuery(id+"F14.wireOp",EDGE,"E4.top"),sQuery(id+"F14.wireOp",EDGE,"E4.left"),sQuery(id+"F14.wireOp",EDGE,"E4.right")])]});
            var Q61;
            Q61=makeQuery(id+"F38.opPattern","COPY",BODY,{"derivedFrom":makeQuery(id+"F13.opPattern","COPY",BODY,{"derivedFrom":makeQuery(id+"F11.opPattern","COPY",BODY,{"derivedFrom":makeQuery(id+"F8.opExtrude","SWEPT_BODY",BODY,{"disambiguationData":[OSD([sQuery(id+"F7.wireOp",EDGE,"E3.bottom"),sQuery(id+"F7.wireOp",EDGE,"E3.top"),sQuery(id+"F7.wireOp",EDGE,"E3.left"),sQuery(id+"F7.wireOp",EDGE,"E3.right")])]}),"instanceName":"1"}),"instanceName":"1"}),"instanceName":"1"});
            var Q62;
            Q62=makeQuery(id+"F38.opPattern","COPY",BODY,{"derivedFrom":makeQuery(id+"F20.opPattern","COPY",BODY,{"derivedFrom":makeQuery(id+"F15.opExtrude","SWEPT_BODY",BODY,{"disambiguationData":[OSD([sQuery(id+"F14.wireOp",EDGE,"E4.bottom"),sQuery(id+"F14.wireOp",EDGE,"E4.top"),sQuery(id+"F14.wireOp",EDGE,"E4.left"),sQuery(id+"F14.wireOp",EDGE,"E4.right")])]}),"instanceName":"1"}),"instanceName":"1"});
            var Q63;
            Q63=makeQuery(id+"F38.opPattern","COPY",EDGE,{"derivedFrom":makeQuery(id+"F19.opPattern","COPY",EDGE,{"derivedFrom":makeQuery(id+"F15.opExtrude","CAP_EDGE",EDGE,{"disambiguationData":[OSD([sQuery(id+"F14.wireOp",EDGE,"E4.left")])],"isStart":false}),"instanceName":"1"}),"instanceName":"1"});
            transform(context, id + "F39", {"entities" : qUnion([Q0, Q1, Q2, Q3, Q4, Q5, Q6, Q7, Q8, Q9, Q10, Q11, Q12, Q13, Q14, Q15, Q16, Q17, Q18, Q19, Q20, Q21, Q22, Q23, Q24, Q25, Q26, Q27, Q28, Q29, Q30, Q31, Q32, Q33, Q34, Q35, Q36, Q37, Q38, Q39, Q40, Q41, Q42, Q43, Q44, Q45, Q46, Q47, Q48, Q49, Q50, Q51, Q52, Q53, Q54, Q55, Q56, Q57, Q58, Q59, Q60, Q61, Q62]), "transformType" : TransformType.ROTATION, "transformAxis" : qUnion([Q63]), "angle" : 180 * degree, "makeCopy" : false});
        }
        {
            var Q0;
            Q0=makeQuery(id+"F2.opExtrude","SWEPT_BODY",BODY,{"disambiguationData":[OSD([sQuery(id+"F1.wireOp",EDGE,"E1.bottom"),sQuery(id+"F1.wireOp",EDGE,"E1.top"),sQuery(id+"F1.wireOp",EDGE,"E1.left"),sQuery(id+"F1.wireOp",EDGE,"E1.right")])]});
            var Q1;
            Q1=makeQuery(id+"F3.opPattern","COPY",BODY,{"derivedFrom":makeQuery(id+"F2.opExtrude","SWEPT_BODY",BODY,{"disambiguationData":[OSD([sQuery(id+"F1.wireOp",EDGE,"E1.bottom"),sQuery(id+"F1.wireOp",EDGE,"E1.top"),sQuery(id+"F1.wireOp",EDGE,"E1.left"),sQuery(id+"F1.wireOp",EDGE,"E1.right")])]}),"instanceName":"1"});
            var Q2;
            Q2=makeQuery(id+"F25.opPattern","COPY",BODY,{"derivedFrom":makeQuery(id+"F24.opPattern","COPY",BODY,{"derivedFrom":makeQuery(id+"F23.opExtrude","SWEPT_BODY",BODY,{"disambiguationData":[OSD([sQuery(id+"F22.wireOp",EDGE,"E5.bottom"),sQuery(id+"F22.wireOp",EDGE,"E5.top"),sQuery(id+"F22.wireOp",EDGE,"E5.left"),sQuery(id+"F22.wireOp",EDGE,"E5.right")])]}),"instanceName":"1"}),"instanceName":"1"});
            var Q3;
            Q3=makeQuery(id+"F24.opPattern","COPY",BODY,{"derivedFrom":makeQuery(id+"F23.opExtrude","SWEPT_BODY",BODY,{"disambiguationData":[OSD([sQuery(id+"F22.wireOp",EDGE,"E5.bottom"),sQuery(id+"F22.wireOp",EDGE,"E5.top"),sQuery(id+"F22.wireOp",EDGE,"E5.left"),sQuery(id+"F22.wireOp",EDGE,"E5.right")])]}),"instanceName":"1"});
            var Q4;
            Q4=makeQuery(id+"F27.opPattern","COPY",BODY,{"derivedFrom":makeQuery(id+"F5.opExtrude","SWEPT_BODY",BODY,{"disambiguationData":[OSD([sQuery(id+"F4.wireOp",EDGE,"E2.bottom"),sQuery(id+"F4.wireOp",EDGE,"E2.top"),sQuery(id+"F4.wireOp",EDGE,"E2.left"),sQuery(id+"F4.wireOp",EDGE,"E2.right")])]}),"instanceName":"1"});
            var Q5;
            Q5=makeQuery(id+"F8.opExtrude","SWEPT_BODY",BODY,{"disambiguationData":[OSD([sQuery(id+"F7.wireOp",EDGE,"E3.bottom"),sQuery(id+"F7.wireOp",EDGE,"E3.top"),sQuery(id+"F7.wireOp",EDGE,"E3.left"),sQuery(id+"F7.wireOp",EDGE,"E3.right")])]});
            var Q6;
            Q6=makeQuery(id+"F20.opPattern","COPY",BODY,{"derivedFrom":makeQuery(id+"F15.opExtrude","SWEPT_BODY",BODY,{"disambiguationData":[OSD([sQuery(id+"F14.wireOp",EDGE,"E4.bottom"),sQuery(id+"F14.wireOp",EDGE,"E4.top"),sQuery(id+"F14.wireOp",EDGE,"E4.left"),sQuery(id+"F14.wireOp",EDGE,"E4.right")])]}),"instanceName":"1"});
            var Q7;
            Q7=makeQuery(id+"F5.opExtrude","SWEPT_BODY",BODY,{"disambiguationData":[OSD([sQuery(id+"F4.wireOp",EDGE,"E2.bottom"),sQuery(id+"F4.wireOp",EDGE,"E2.top"),sQuery(id+"F4.wireOp",EDGE,"E2.left"),sQuery(id+"F4.wireOp",EDGE,"E2.right")])]});
            var Q8;
            Q8=makeQuery(id+"F13.opPattern","COPY",BODY,{"derivedFrom":makeQuery(id+"F10.opPattern","COPY",BODY,{"derivedFrom":makeQuery(id+"F8.opExtrude","SWEPT_BODY",BODY,{"disambiguationData":[OSD([sQuery(id+"F7.wireOp",EDGE,"E3.bottom"),sQuery(id+"F7.wireOp",EDGE,"E3.top"),sQuery(id+"F7.wireOp",EDGE,"E3.left"),sQuery(id+"F7.wireOp",EDGE,"E3.right")])]}),"instanceName":"1"}),"instanceName":"1"});
            var Q9;
            Q9=makeQuery(id+"F31.opPattern","COPY",BODY,{"derivedFrom":makeQuery(id+"F2.opExtrude","SWEPT_BODY",BODY,{"disambiguationData":[OSD([sQuery(id+"F1.wireOp",EDGE,"E1.bottom"),sQuery(id+"F1.wireOp",EDGE,"E1.top"),sQuery(id+"F1.wireOp",EDGE,"E1.left"),sQuery(id+"F1.wireOp",EDGE,"E1.right")])]}),"instanceName":"1"});
            var Q10;
            Q10=makeQuery(id+"F29.opPattern","COPY",BODY,{"derivedFrom":makeQuery(id+"F27.opPattern","COPY",BODY,{"derivedFrom":makeQuery(id+"F5.opExtrude","SWEPT_BODY",BODY,{"disambiguationData":[OSD([sQuery(id+"F4.wireOp",EDGE,"E2.bottom"),sQuery(id+"F4.wireOp",EDGE,"E2.top"),sQuery(id+"F4.wireOp",EDGE,"E2.left"),sQuery(id+"F4.wireOp",EDGE,"E2.right")])]}),"instanceName":"1"}),"instanceName":"1"});
            var Q11;
            Q11=makeQuery(id+"F35.opPattern","COPY",BODY,{"derivedFrom":makeQuery(id+"F31.opPattern","COPY",BODY,{"derivedFrom":makeQuery(id+"F2.opExtrude","SWEPT_BODY",BODY,{"disambiguationData":[OSD([sQuery(id+"F1.wireOp",EDGE,"E1.bottom"),sQuery(id+"F1.wireOp",EDGE,"E1.top"),sQuery(id+"F1.wireOp",EDGE,"E1.left"),sQuery(id+"F1.wireOp",EDGE,"E1.right")])]}),"instanceName":"1"}),"instanceName":"1"});
            var Q12;
            Q12=makeQuery(id+"F23.opExtrude","SWEPT_BODY",BODY,{"disambiguationData":[OSD([sQuery(id+"F22.wireOp",EDGE,"E5.bottom"),sQuery(id+"F22.wireOp",EDGE,"E5.top"),sQuery(id+"F22.wireOp",EDGE,"E5.left"),sQuery(id+"F22.wireOp",EDGE,"E5.right")])]});
            var Q13;
            Q13=makeQuery(id+"F35.opPattern","COPY",BODY,{"derivedFrom":makeQuery(id+"F25.opPattern","COPY",BODY,{"derivedFrom":makeQuery(id+"F24.opPattern","COPY",BODY,{"derivedFrom":makeQuery(id+"F23.opExtrude","SWEPT_BODY",BODY,{"disambiguationData":[OSD([sQuery(id+"F22.wireOp",EDGE,"E5.bottom"),sQuery(id+"F22.wireOp",EDGE,"E5.top"),sQuery(id+"F22.wireOp",EDGE,"E5.left"),sQuery(id+"F22.wireOp",EDGE,"E5.right")])]}),"instanceName":"1"}),"instanceName":"1"}),"instanceName":"1"});
            var Q14;
            Q14=makeQuery(id+"F30.opPattern","COPY",BODY,{"derivedFrom":makeQuery(id+"F29.opPattern","COPY",BODY,{"derivedFrom":makeQuery(id+"F27.opPattern","COPY",BODY,{"derivedFrom":makeQuery(id+"F5.opExtrude","SWEPT_BODY",BODY,{"disambiguationData":[OSD([sQuery(id+"F4.wireOp",EDGE,"E2.bottom"),sQuery(id+"F4.wireOp",EDGE,"E2.top"),sQuery(id+"F4.wireOp",EDGE,"E2.left"),sQuery(id+"F4.wireOp",EDGE,"E2.right")])]}),"instanceName":"1"}),"instanceName":"1"}),"instanceName":"1"});
            var Q15;
            Q15=makeQuery(id+"F11.opPattern","COPY",BODY,{"derivedFrom":makeQuery(id+"F8.opExtrude","SWEPT_BODY",BODY,{"disambiguationData":[OSD([sQuery(id+"F7.wireOp",EDGE,"E3.bottom"),sQuery(id+"F7.wireOp",EDGE,"E3.top"),sQuery(id+"F7.wireOp",EDGE,"E3.left"),sQuery(id+"F7.wireOp",EDGE,"E3.right")])]}),"instanceName":"1"});
            var Q16;
            Q16=makeQuery(id+"F10.opPattern","COPY",BODY,{"derivedFrom":makeQuery(id+"F8.opExtrude","SWEPT_BODY",BODY,{"disambiguationData":[OSD([sQuery(id+"F7.wireOp",EDGE,"E3.bottom"),sQuery(id+"F7.wireOp",EDGE,"E3.top"),sQuery(id+"F7.wireOp",EDGE,"E3.left"),sQuery(id+"F7.wireOp",EDGE,"E3.right")])]}),"instanceName":"1"});
            var Q17;
            Q17=makeQuery(id+"F6.opPattern","COPY",BODY,{"derivedFrom":makeQuery(id+"F5.opExtrude","SWEPT_BODY",BODY,{"disambiguationData":[OSD([sQuery(id+"F4.wireOp",EDGE,"E2.bottom"),sQuery(id+"F4.wireOp",EDGE,"E2.top"),sQuery(id+"F4.wireOp",EDGE,"E2.left"),sQuery(id+"F4.wireOp",EDGE,"E2.right")])]}),"instanceName":"1"});
            var Q18;
            Q18=makeQuery(id+"F35.opPattern","COPY",BODY,{"derivedFrom":makeQuery(id+"F27.opPattern","COPY",BODY,{"derivedFrom":makeQuery(id+"F5.opExtrude","SWEPT_BODY",BODY,{"disambiguationData":[OSD([sQuery(id+"F4.wireOp",EDGE,"E2.bottom"),sQuery(id+"F4.wireOp",EDGE,"E2.top"),sQuery(id+"F4.wireOp",EDGE,"E2.left"),sQuery(id+"F4.wireOp",EDGE,"E2.right")])]}),"instanceName":"1"}),"instanceName":"1"});
            var Q19;
            Q19=makeQuery(id+"F35.opPattern","COPY",BODY,{"derivedFrom":makeQuery(id+"F29.opPattern","COPY",BODY,{"derivedFrom":makeQuery(id+"F27.opPattern","COPY",BODY,{"derivedFrom":makeQuery(id+"F5.opExtrude","SWEPT_BODY",BODY,{"disambiguationData":[OSD([sQuery(id+"F4.wireOp",EDGE,"E2.bottom"),sQuery(id+"F4.wireOp",EDGE,"E2.top"),sQuery(id+"F4.wireOp",EDGE,"E2.left"),sQuery(id+"F4.wireOp",EDGE,"E2.right")])]}),"instanceName":"1"}),"instanceName":"1"}),"instanceName":"1"});
            var Q20;
            Q20=makeQuery(id+"F35.opPattern","COPY",BODY,{"derivedFrom":makeQuery(id+"F30.opPattern","COPY",BODY,{"derivedFrom":makeQuery(id+"F29.opPattern","COPY",BODY,{"derivedFrom":makeQuery(id+"F27.opPattern","COPY",BODY,{"derivedFrom":makeQuery(id+"F5.opExtrude","SWEPT_BODY",BODY,{"disambiguationData":[OSD([sQuery(id+"F4.wireOp",EDGE,"E2.bottom"),sQuery(id+"F4.wireOp",EDGE,"E2.top"),sQuery(id+"F4.wireOp",EDGE,"E2.left"),sQuery(id+"F4.wireOp",EDGE,"E2.right")])]}),"instanceName":"1"}),"instanceName":"1"}),"instanceName":"1"}),"instanceName":"1"});
            var Q21;
            Q21=makeQuery(id+"F33.opPattern","COPY",BODY,{"derivedFrom":makeQuery(id+"F31.opPattern","COPY",BODY,{"derivedFrom":makeQuery(id+"F2.opExtrude","SWEPT_BODY",BODY,{"disambiguationData":[OSD([sQuery(id+"F1.wireOp",EDGE,"E1.bottom"),sQuery(id+"F1.wireOp",EDGE,"E1.top"),sQuery(id+"F1.wireOp",EDGE,"E1.left"),sQuery(id+"F1.wireOp",EDGE,"E1.right")])]}),"instanceName":"1"}),"instanceName":"1"});
            var Q22;
            Q22=makeQuery(id+"F35.opPattern","COPY",BODY,{"derivedFrom":makeQuery(id+"F33.opPattern","COPY",BODY,{"derivedFrom":makeQuery(id+"F31.opPattern","COPY",BODY,{"derivedFrom":makeQuery(id+"F2.opExtrude","SWEPT_BODY",BODY,{"disambiguationData":[OSD([sQuery(id+"F1.wireOp",EDGE,"E1.bottom"),sQuery(id+"F1.wireOp",EDGE,"E1.top"),sQuery(id+"F1.wireOp",EDGE,"E1.left"),sQuery(id+"F1.wireOp",EDGE,"E1.right")])]}),"instanceName":"1"}),"instanceName":"1"}),"instanceName":"1"});
            var Q23;
            Q23=makeQuery(id+"F35.opPattern","COPY",BODY,{"derivedFrom":makeQuery(id+"F24.opPattern","COPY",BODY,{"derivedFrom":makeQuery(id+"F23.opExtrude","SWEPT_BODY",BODY,{"disambiguationData":[OSD([sQuery(id+"F22.wireOp",EDGE,"E5.bottom"),sQuery(id+"F22.wireOp",EDGE,"E5.top"),sQuery(id+"F22.wireOp",EDGE,"E5.left"),sQuery(id+"F22.wireOp",EDGE,"E5.right")])]}),"instanceName":"1"}),"instanceName":"1"});
            var Q24;
            Q24=makeQuery(id+"F35.opPattern","COPY",BODY,{"derivedFrom":makeQuery(id+"F23.opExtrude","SWEPT_BODY",BODY,{"disambiguationData":[OSD([sQuery(id+"F22.wireOp",EDGE,"E5.bottom"),sQuery(id+"F22.wireOp",EDGE,"E5.top"),sQuery(id+"F22.wireOp",EDGE,"E5.left"),sQuery(id+"F22.wireOp",EDGE,"E5.right")])]}),"instanceName":"1"});
            var Q25;
            Q25=makeQuery(id+"F35.opPattern","COPY",BODY,{"derivedFrom":makeQuery(id+"F20.opPattern","COPY",BODY,{"derivedFrom":makeQuery(id+"F15.opExtrude","SWEPT_BODY",BODY,{"disambiguationData":[OSD([sQuery(id+"F14.wireOp",EDGE,"E4.bottom"),sQuery(id+"F14.wireOp",EDGE,"E4.top"),sQuery(id+"F14.wireOp",EDGE,"E4.left"),sQuery(id+"F14.wireOp",EDGE,"E4.right")])]}),"instanceName":"1"}),"instanceName":"1"});
            var Q26;
            Q26=makeQuery(id+"F35.opPattern","COPY",BODY,{"derivedFrom":makeQuery(id+"F19.opPattern","COPY",BODY,{"derivedFrom":makeQuery(id+"F15.opExtrude","SWEPT_BODY",BODY,{"disambiguationData":[OSD([sQuery(id+"F14.wireOp",EDGE,"E4.bottom"),sQuery(id+"F14.wireOp",EDGE,"E4.top"),sQuery(id+"F14.wireOp",EDGE,"E4.left"),sQuery(id+"F14.wireOp",EDGE,"E4.right")])]}),"instanceName":"1"}),"instanceName":"1"});
            var Q27;
            Q27=makeQuery(id+"F35.opPattern","COPY",BODY,{"derivedFrom":makeQuery(id+"F15.opExtrude","SWEPT_BODY",BODY,{"disambiguationData":[OSD([sQuery(id+"F14.wireOp",EDGE,"E4.bottom"),sQuery(id+"F14.wireOp",EDGE,"E4.top"),sQuery(id+"F14.wireOp",EDGE,"E4.left"),sQuery(id+"F14.wireOp",EDGE,"E4.right")])]}),"instanceName":"1"});
            var Q28;
            Q28=makeQuery(id+"F35.opPattern","COPY",BODY,{"derivedFrom":makeQuery(id+"F13.opPattern","COPY",BODY,{"derivedFrom":makeQuery(id+"F11.opPattern","COPY",BODY,{"derivedFrom":makeQuery(id+"F8.opExtrude","SWEPT_BODY",BODY,{"disambiguationData":[OSD([sQuery(id+"F7.wireOp",EDGE,"E3.bottom"),sQuery(id+"F7.wireOp",EDGE,"E3.top"),sQuery(id+"F7.wireOp",EDGE,"E3.left"),sQuery(id+"F7.wireOp",EDGE,"E3.right")])]}),"instanceName":"1"}),"instanceName":"1"}),"instanceName":"1"});
            var Q29;
            Q29=makeQuery(id+"F35.opPattern","COPY",BODY,{"derivedFrom":makeQuery(id+"F6.opPattern","COPY",BODY,{"derivedFrom":makeQuery(id+"F5.opExtrude","SWEPT_BODY",BODY,{"disambiguationData":[OSD([sQuery(id+"F4.wireOp",EDGE,"E2.bottom"),sQuery(id+"F4.wireOp",EDGE,"E2.top"),sQuery(id+"F4.wireOp",EDGE,"E2.left"),sQuery(id+"F4.wireOp",EDGE,"E2.right")])]}),"instanceName":"1"}),"instanceName":"1"});
            var Q30;
            Q30=makeQuery(id+"F35.opPattern","COPY",BODY,{"derivedFrom":makeQuery(id+"F3.opPattern","COPY",BODY,{"derivedFrom":makeQuery(id+"F2.opExtrude","SWEPT_BODY",BODY,{"disambiguationData":[OSD([sQuery(id+"F1.wireOp",EDGE,"E1.bottom"),sQuery(id+"F1.wireOp",EDGE,"E1.top"),sQuery(id+"F1.wireOp",EDGE,"E1.left"),sQuery(id+"F1.wireOp",EDGE,"E1.right")])]}),"instanceName":"1"}),"instanceName":"1"});
            var Q31;
            Q31=makeQuery(id+"F35.opPattern","COPY",BODY,{"derivedFrom":makeQuery(id+"F2.opExtrude","SWEPT_BODY",BODY,{"disambiguationData":[OSD([sQuery(id+"F1.wireOp",EDGE,"E1.bottom"),sQuery(id+"F1.wireOp",EDGE,"E1.top"),sQuery(id+"F1.wireOp",EDGE,"E1.left"),sQuery(id+"F1.wireOp",EDGE,"E1.right")])]}),"instanceName":"1"});
            var Q32;
            Q32=makeQuery(id+"F35.opPattern","COPY",BODY,{"derivedFrom":makeQuery(id+"F10.opPattern","COPY",BODY,{"derivedFrom":makeQuery(id+"F8.opExtrude","SWEPT_BODY",BODY,{"disambiguationData":[OSD([sQuery(id+"F7.wireOp",EDGE,"E3.bottom"),sQuery(id+"F7.wireOp",EDGE,"E3.top"),sQuery(id+"F7.wireOp",EDGE,"E3.left"),sQuery(id+"F7.wireOp",EDGE,"E3.right")])]}),"instanceName":"1"}),"instanceName":"1"});
            var Q33;
            Q33=makeQuery(id+"F35.opPattern","COPY",BODY,{"derivedFrom":makeQuery(id+"F13.opPattern","COPY",BODY,{"derivedFrom":makeQuery(id+"F8.opExtrude","SWEPT_BODY",BODY,{"disambiguationData":[OSD([sQuery(id+"F7.wireOp",EDGE,"E3.bottom"),sQuery(id+"F7.wireOp",EDGE,"E3.top"),sQuery(id+"F7.wireOp",EDGE,"E3.left"),sQuery(id+"F7.wireOp",EDGE,"E3.right")])]}),"instanceName":"1"}),"instanceName":"1"});
            var Q34;
            Q34=makeQuery(id+"F35.opPattern","COPY",BODY,{"derivedFrom":makeQuery(id+"F13.opPattern","COPY",BODY,{"derivedFrom":makeQuery(id+"F10.opPattern","COPY",BODY,{"derivedFrom":makeQuery(id+"F8.opExtrude","SWEPT_BODY",BODY,{"disambiguationData":[OSD([sQuery(id+"F7.wireOp",EDGE,"E3.bottom"),sQuery(id+"F7.wireOp",EDGE,"E3.top"),sQuery(id+"F7.wireOp",EDGE,"E3.left"),sQuery(id+"F7.wireOp",EDGE,"E3.right")])]}),"instanceName":"1"}),"instanceName":"1"}),"instanceName":"1"});
            var Q35;
            Q35=makeQuery(id+"F38.opPattern","COPY",BODY,{"derivedFrom":makeQuery(id+"F6.opPattern","COPY",BODY,{"derivedFrom":makeQuery(id+"F5.opExtrude","SWEPT_BODY",BODY,{"disambiguationData":[OSD([sQuery(id+"F4.wireOp",EDGE,"E2.bottom"),sQuery(id+"F4.wireOp",EDGE,"E2.top"),sQuery(id+"F4.wireOp",EDGE,"E2.left"),sQuery(id+"F4.wireOp",EDGE,"E2.right")])]}),"instanceName":"1"}),"instanceName":"1"});
            var Q36;
            Q36=makeQuery(id+"F38.opPattern","COPY",BODY,{"derivedFrom":makeQuery(id+"F2.opExtrude","SWEPT_BODY",BODY,{"disambiguationData":[OSD([sQuery(id+"F1.wireOp",EDGE,"E1.bottom"),sQuery(id+"F1.wireOp",EDGE,"E1.top"),sQuery(id+"F1.wireOp",EDGE,"E1.left"),sQuery(id+"F1.wireOp",EDGE,"E1.right")])]}),"instanceName":"1"});
            var Q37;
            Q37=makeQuery(id+"F38.opPattern","COPY",BODY,{"derivedFrom":makeQuery(id+"F3.opPattern","COPY",BODY,{"derivedFrom":makeQuery(id+"F2.opExtrude","SWEPT_BODY",BODY,{"disambiguationData":[OSD([sQuery(id+"F1.wireOp",EDGE,"E1.bottom"),sQuery(id+"F1.wireOp",EDGE,"E1.top"),sQuery(id+"F1.wireOp",EDGE,"E1.left"),sQuery(id+"F1.wireOp",EDGE,"E1.right")])]}),"instanceName":"1"}),"instanceName":"1"});
            var Q38;
            Q38=makeQuery(id+"F38.opPattern","COPY",BODY,{"derivedFrom":makeQuery(id+"F8.opExtrude","SWEPT_BODY",BODY,{"disambiguationData":[OSD([sQuery(id+"F7.wireOp",EDGE,"E3.bottom"),sQuery(id+"F7.wireOp",EDGE,"E3.top"),sQuery(id+"F7.wireOp",EDGE,"E3.left"),sQuery(id+"F7.wireOp",EDGE,"E3.right")])]}),"instanceName":"1"});
            var Q39;
            Q39=makeQuery(id+"F38.opPattern","COPY",BODY,{"derivedFrom":makeQuery(id+"F10.opPattern","COPY",BODY,{"derivedFrom":makeQuery(id+"F8.opExtrude","SWEPT_BODY",BODY,{"disambiguationData":[OSD([sQuery(id+"F7.wireOp",EDGE,"E3.bottom"),sQuery(id+"F7.wireOp",EDGE,"E3.top"),sQuery(id+"F7.wireOp",EDGE,"E3.left"),sQuery(id+"F7.wireOp",EDGE,"E3.right")])]}),"instanceName":"1"}),"instanceName":"1"});
            var Q40;
            Q40=makeQuery(id+"F38.opPattern","COPY",BODY,{"derivedFrom":makeQuery(id+"F11.opPattern","COPY",BODY,{"derivedFrom":makeQuery(id+"F8.opExtrude","SWEPT_BODY",BODY,{"disambiguationData":[OSD([sQuery(id+"F7.wireOp",EDGE,"E3.bottom"),sQuery(id+"F7.wireOp",EDGE,"E3.top"),sQuery(id+"F7.wireOp",EDGE,"E3.left"),sQuery(id+"F7.wireOp",EDGE,"E3.right")])]}),"instanceName":"1"}),"instanceName":"1"});
            var Q41;
            Q41=makeQuery(id+"F38.opPattern","COPY",BODY,{"derivedFrom":makeQuery(id+"F13.opPattern","COPY",BODY,{"derivedFrom":makeQuery(id+"F10.opPattern","COPY",BODY,{"derivedFrom":makeQuery(id+"F8.opExtrude","SWEPT_BODY",BODY,{"disambiguationData":[OSD([sQuery(id+"F7.wireOp",EDGE,"E3.bottom"),sQuery(id+"F7.wireOp",EDGE,"E3.top"),sQuery(id+"F7.wireOp",EDGE,"E3.left"),sQuery(id+"F7.wireOp",EDGE,"E3.right")])]}),"instanceName":"1"}),"instanceName":"1"}),"instanceName":"1"});
            var Q42;
            Q42=makeQuery(id+"F38.opPattern","COPY",BODY,{"derivedFrom":makeQuery(id+"F20.opPattern","COPY",BODY,{"derivedFrom":makeQuery(id+"F15.opExtrude","SWEPT_BODY",BODY,{"disambiguationData":[OSD([sQuery(id+"F14.wireOp",EDGE,"E4.bottom"),sQuery(id+"F14.wireOp",EDGE,"E4.top"),sQuery(id+"F14.wireOp",EDGE,"E4.left"),sQuery(id+"F14.wireOp",EDGE,"E4.right")])]}),"instanceName":"1"}),"instanceName":"1"});
            var Q43;
            Q43=makeQuery(id+"F38.opPattern","COPY",BODY,{"derivedFrom":makeQuery(id+"F23.opExtrude","SWEPT_BODY",BODY,{"disambiguationData":[OSD([sQuery(id+"F22.wireOp",EDGE,"E5.bottom"),sQuery(id+"F22.wireOp",EDGE,"E5.top"),sQuery(id+"F22.wireOp",EDGE,"E5.left"),sQuery(id+"F22.wireOp",EDGE,"E5.right")])]}),"instanceName":"1"});
            var Q44;
            Q44=makeQuery(id+"F38.opPattern","COPY",BODY,{"derivedFrom":makeQuery(id+"F24.opPattern","COPY",BODY,{"derivedFrom":makeQuery(id+"F23.opExtrude","SWEPT_BODY",BODY,{"disambiguationData":[OSD([sQuery(id+"F22.wireOp",EDGE,"E5.bottom"),sQuery(id+"F22.wireOp",EDGE,"E5.top"),sQuery(id+"F22.wireOp",EDGE,"E5.left"),sQuery(id+"F22.wireOp",EDGE,"E5.right")])]}),"instanceName":"1"}),"instanceName":"1"});
            var Q45;
            Q45=makeQuery(id+"F38.opPattern","COPY",BODY,{"derivedFrom":makeQuery(id+"F25.opPattern","COPY",BODY,{"derivedFrom":makeQuery(id+"F24.opPattern","COPY",BODY,{"derivedFrom":makeQuery(id+"F23.opExtrude","SWEPT_BODY",BODY,{"disambiguationData":[OSD([sQuery(id+"F22.wireOp",EDGE,"E5.bottom"),sQuery(id+"F22.wireOp",EDGE,"E5.top"),sQuery(id+"F22.wireOp",EDGE,"E5.left"),sQuery(id+"F22.wireOp",EDGE,"E5.right")])]}),"instanceName":"1"}),"instanceName":"1"}),"instanceName":"1"});
            var Q46;
            Q46=makeQuery(id+"F38.opPattern","COPY",BODY,{"derivedFrom":makeQuery(id+"F27.opPattern","COPY",BODY,{"derivedFrom":makeQuery(id+"F5.opExtrude","SWEPT_BODY",BODY,{"disambiguationData":[OSD([sQuery(id+"F4.wireOp",EDGE,"E2.bottom"),sQuery(id+"F4.wireOp",EDGE,"E2.top"),sQuery(id+"F4.wireOp",EDGE,"E2.left"),sQuery(id+"F4.wireOp",EDGE,"E2.right")])]}),"instanceName":"1"}),"instanceName":"1"});
            var Q47;
            Q47=makeQuery(id+"F38.opPattern","COPY",BODY,{"derivedFrom":makeQuery(id+"F29.opPattern","COPY",BODY,{"derivedFrom":makeQuery(id+"F27.opPattern","COPY",BODY,{"derivedFrom":makeQuery(id+"F5.opExtrude","SWEPT_BODY",BODY,{"disambiguationData":[OSD([sQuery(id+"F4.wireOp",EDGE,"E2.bottom"),sQuery(id+"F4.wireOp",EDGE,"E2.top"),sQuery(id+"F4.wireOp",EDGE,"E2.left"),sQuery(id+"F4.wireOp",EDGE,"E2.right")])]}),"instanceName":"1"}),"instanceName":"1"}),"instanceName":"1"});
            var Q48;
            Q48=makeQuery(id+"F38.opPattern","COPY",BODY,{"derivedFrom":makeQuery(id+"F30.opPattern","COPY",BODY,{"derivedFrom":makeQuery(id+"F29.opPattern","COPY",BODY,{"derivedFrom":makeQuery(id+"F27.opPattern","COPY",BODY,{"derivedFrom":makeQuery(id+"F5.opExtrude","SWEPT_BODY",BODY,{"disambiguationData":[OSD([sQuery(id+"F4.wireOp",EDGE,"E2.bottom"),sQuery(id+"F4.wireOp",EDGE,"E2.top"),sQuery(id+"F4.wireOp",EDGE,"E2.left"),sQuery(id+"F4.wireOp",EDGE,"E2.right")])]}),"instanceName":"1"}),"instanceName":"1"}),"instanceName":"1"}),"instanceName":"1"});
            var Q49;
            Q49=makeQuery(id+"F38.opPattern","COPY",BODY,{"derivedFrom":makeQuery(id+"F31.opPattern","COPY",BODY,{"derivedFrom":makeQuery(id+"F2.opExtrude","SWEPT_BODY",BODY,{"disambiguationData":[OSD([sQuery(id+"F1.wireOp",EDGE,"E1.bottom"),sQuery(id+"F1.wireOp",EDGE,"E1.top"),sQuery(id+"F1.wireOp",EDGE,"E1.left"),sQuery(id+"F1.wireOp",EDGE,"E1.right")])]}),"instanceName":"1"}),"instanceName":"1"});
            var Q50;
            Q50=makeQuery(id+"F38.opPattern","COPY",BODY,{"derivedFrom":makeQuery(id+"F33.opPattern","COPY",BODY,{"derivedFrom":makeQuery(id+"F31.opPattern","COPY",BODY,{"derivedFrom":makeQuery(id+"F2.opExtrude","SWEPT_BODY",BODY,{"disambiguationData":[OSD([sQuery(id+"F1.wireOp",EDGE,"E1.bottom"),sQuery(id+"F1.wireOp",EDGE,"E1.top"),sQuery(id+"F1.wireOp",EDGE,"E1.left"),sQuery(id+"F1.wireOp",EDGE,"E1.right")])]}),"instanceName":"1"}),"instanceName":"1"}),"instanceName":"1"});
            var Q51;
            Q51=makeQuery(id+"F13.opPattern","COPY",BODY,{"derivedFrom":makeQuery(id+"F8.opExtrude","SWEPT_BODY",BODY,{"disambiguationData":[OSD([sQuery(id+"F7.wireOp",EDGE,"E3.bottom"),sQuery(id+"F7.wireOp",EDGE,"E3.top"),sQuery(id+"F7.wireOp",EDGE,"E3.left"),sQuery(id+"F7.wireOp",EDGE,"E3.right")])]}),"instanceName":"1"});
            var Q52;
            Q52=makeQuery(id+"F13.opPattern","COPY",BODY,{"derivedFrom":makeQuery(id+"F11.opPattern","COPY",BODY,{"derivedFrom":makeQuery(id+"F8.opExtrude","SWEPT_BODY",BODY,{"disambiguationData":[OSD([sQuery(id+"F7.wireOp",EDGE,"E3.bottom"),sQuery(id+"F7.wireOp",EDGE,"E3.top"),sQuery(id+"F7.wireOp",EDGE,"E3.left"),sQuery(id+"F7.wireOp",EDGE,"E3.right")])]}),"instanceName":"1"}),"instanceName":"1"});
            var Q53;
            Q53=makeQuery(id+"F35.opPattern","COPY",BODY,{"derivedFrom":makeQuery(id+"F5.opExtrude","SWEPT_BODY",BODY,{"disambiguationData":[OSD([sQuery(id+"F4.wireOp",EDGE,"E2.bottom"),sQuery(id+"F4.wireOp",EDGE,"E2.top"),sQuery(id+"F4.wireOp",EDGE,"E2.left"),sQuery(id+"F4.wireOp",EDGE,"E2.right")])]}),"instanceName":"1"});
            var Q54;
            Q54=makeQuery(id+"F38.opPattern","COPY",BODY,{"derivedFrom":makeQuery(id+"F5.opExtrude","SWEPT_BODY",BODY,{"disambiguationData":[OSD([sQuery(id+"F4.wireOp",EDGE,"E2.bottom"),sQuery(id+"F4.wireOp",EDGE,"E2.top"),sQuery(id+"F4.wireOp",EDGE,"E2.left"),sQuery(id+"F4.wireOp",EDGE,"E2.right")])]}),"instanceName":"1"});
            var Q55;
            Q55=makeQuery(id+"F38.opPattern","COPY",BODY,{"derivedFrom":makeQuery(id+"F13.opPattern","COPY",BODY,{"derivedFrom":makeQuery(id+"F8.opExtrude","SWEPT_BODY",BODY,{"disambiguationData":[OSD([sQuery(id+"F7.wireOp",EDGE,"E3.bottom"),sQuery(id+"F7.wireOp",EDGE,"E3.top"),sQuery(id+"F7.wireOp",EDGE,"E3.left"),sQuery(id+"F7.wireOp",EDGE,"E3.right")])]}),"instanceName":"1"}),"instanceName":"1"});
            var Q56;
            Q56=makeQuery(id+"F38.opPattern","COPY",BODY,{"derivedFrom":makeQuery(id+"F13.opPattern","COPY",BODY,{"derivedFrom":makeQuery(id+"F11.opPattern","COPY",BODY,{"derivedFrom":makeQuery(id+"F8.opExtrude","SWEPT_BODY",BODY,{"disambiguationData":[OSD([sQuery(id+"F7.wireOp",EDGE,"E3.bottom"),sQuery(id+"F7.wireOp",EDGE,"E3.top"),sQuery(id+"F7.wireOp",EDGE,"E3.left"),sQuery(id+"F7.wireOp",EDGE,"E3.right")])]}),"instanceName":"1"}),"instanceName":"1"}),"instanceName":"1"});
            var Q57;
            Q57=makeQuery(id+"F38.opPattern","COPY",BODY,{"derivedFrom":makeQuery(id+"F15.opExtrude","SWEPT_BODY",BODY,{"disambiguationData":[OSD([sQuery(id+"F14.wireOp",EDGE,"E4.bottom"),sQuery(id+"F14.wireOp",EDGE,"E4.top"),sQuery(id+"F14.wireOp",EDGE,"E4.left"),sQuery(id+"F14.wireOp",EDGE,"E4.right")])]}),"instanceName":"1"});
            var Q58;
            Q58=makeQuery(id+"F38.opPattern","COPY",BODY,{"derivedFrom":makeQuery(id+"F19.opPattern","COPY",BODY,{"derivedFrom":makeQuery(id+"F15.opExtrude","SWEPT_BODY",BODY,{"disambiguationData":[OSD([sQuery(id+"F14.wireOp",EDGE,"E4.bottom"),sQuery(id+"F14.wireOp",EDGE,"E4.top"),sQuery(id+"F14.wireOp",EDGE,"E4.left"),sQuery(id+"F14.wireOp",EDGE,"E4.right")])]}),"instanceName":"1"}),"instanceName":"1"});
            var Q59;
            Q59=makeQuery(id+"F15.opExtrude","SWEPT_BODY",BODY,{"disambiguationData":[OSD([sQuery(id+"F14.wireOp",EDGE,"E4.bottom"),sQuery(id+"F14.wireOp",EDGE,"E4.top"),sQuery(id+"F14.wireOp",EDGE,"E4.left"),sQuery(id+"F14.wireOp",EDGE,"E4.right")])]});
            var Q60;
            Q60=makeQuery(id+"F19.opPattern","COPY",BODY,{"derivedFrom":makeQuery(id+"F15.opExtrude","SWEPT_BODY",BODY,{"disambiguationData":[OSD([sQuery(id+"F14.wireOp",EDGE,"E4.bottom"),sQuery(id+"F14.wireOp",EDGE,"E4.top"),sQuery(id+"F14.wireOp",EDGE,"E4.left"),sQuery(id+"F14.wireOp",EDGE,"E4.right")])]}),"instanceName":"1"});
            var Q61;
            Q61=makeQuery(id+"F35.opPattern","COPY",BODY,{"derivedFrom":makeQuery(id+"F8.opExtrude","SWEPT_BODY",BODY,{"disambiguationData":[OSD([sQuery(id+"F7.wireOp",EDGE,"E3.bottom"),sQuery(id+"F7.wireOp",EDGE,"E3.top"),sQuery(id+"F7.wireOp",EDGE,"E3.left"),sQuery(id+"F7.wireOp",EDGE,"E3.right")])]}),"instanceName":"1"});
            var Q62;
            Q62=makeQuery(id+"F35.opPattern","COPY",BODY,{"derivedFrom":makeQuery(id+"F11.opPattern","COPY",BODY,{"derivedFrom":makeQuery(id+"F8.opExtrude","SWEPT_BODY",BODY,{"disambiguationData":[OSD([sQuery(id+"F7.wireOp",EDGE,"E3.bottom"),sQuery(id+"F7.wireOp",EDGE,"E3.top"),sQuery(id+"F7.wireOp",EDGE,"E3.left"),sQuery(id+"F7.wireOp",EDGE,"E3.right")])]}),"instanceName":"1"}),"instanceName":"1"});
            var Q63;
            Q63=makeQuery(id+"F35.opPattern","COPY",EDGE,{"derivedFrom":makeQuery(id+"F30.opPattern","COPY",EDGE,{"derivedFrom":makeQuery(id+"F29.opPattern","COPY",EDGE,{"derivedFrom":makeQuery(id+"F27.opPattern","COPY",EDGE,{"derivedFrom":makeQuery(id+"F5.opExtrude","CAP_EDGE",EDGE,{"disambiguationData":[OSD([sQuery(id+"F4.wireOp",EDGE,"E2.top")])],"isStart":false}),"instanceName":"1"}),"instanceName":"1"}),"instanceName":"1"}),"instanceName":"1"});
            transform(context, id + "F40", {"entities" : qUnion([Q0, Q1, Q2, Q3, Q4, Q5, Q6, Q7, Q8, Q9, Q10, Q11, Q12, Q13, Q14, Q15, Q16, Q17, Q18, Q19, Q20, Q21, Q22, Q23, Q24, Q25, Q26, Q27, Q28, Q29, Q30, Q31, Q32, Q33, Q34, Q35, Q36, Q37, Q38, Q39, Q40, Q41, Q42, Q43, Q44, Q45, Q46, Q47, Q48, Q49, Q50, Q51, Q52, Q53, Q54, Q55, Q56, Q57, Q58, Q59, Q60, Q61, Q62]), "transformType" : TransformType.TRANSLATION_DISTANCE, "transformDirection" : qUnion([Q63]), "distance" : 1210 * mm, "oppositeDirection" : true, "makeCopy" : false});
        }
        {
            var Q0;
            Q0=qCreatedBy(makeId("Right.planeOp"),FACE);
            var sketch = newSketch(context, id + "F41", { "sketchPlane" : qUnion([Q0])});
            skLineSegment(sketch, "E6.bottom", {"start": v(-541.55, 302.22) * mm, "end": v(255.63, 302.22) * mm});
            skLineSegment(sketch, "E6.top", {"start": v(-541.55, 424.36) * mm, "end": v(255.63, 424.36) * mm});
            skLineSegment(sketch, "E6.left", {"start": v(-541.55, 302.22) * mm, "end": v(-541.55, 424.36) * mm});
            skLineSegment(sketch, "E6.right", {"start": v(255.63, 302.22) * mm, "end": v(255.63, 424.36) * mm});
            skSolve(sketch);
        }
        {
            var Q0;
            Q0=makeQuery(id+"F41.imprint","IMPRINT",FACE,{"disambiguationData":[TD([[makeQuery(id+"F41.imprint","IMPRINT",EDGE,{"derivedFrom":sQuery(id+"F41.wireOp",EDGE,"E6.bottom")}),1.0]])]});
            extrude(context, id + "F42", {"entities" : qUnion([Q0]), "endBound" : BoundingType.SYMMETRIC, "depth" : 1200 * mm});
        }
        {
            var Q0;
            Q0=makeQuery(id+"F42.opExtrude","SWEPT_FACE",FACE,{"disambiguationData":[OSD([sQuery(id+"F41.wireOp",EDGE,"E6.left")])]});
            var Q1;
            Q1=makeQuery(id+"F42.opExtrude","CAP_FACE",FACE,{"disambiguationData":[OSD([sQuery(id+"F41.wireOp",EDGE,"E6.bottom"),sQuery(id+"F41.wireOp",EDGE,"E6.top"),sQuery(id+"F41.wireOp",EDGE,"E6.left"),sQuery(id+"F41.wireOp",EDGE,"E6.right")])],"isStart":false});
            var Q2;
            Q2=makeQuery(id+"F42.opExtrude","CAP_FACE",FACE,{"disambiguationData":[OSD([sQuery(id+"F41.wireOp",EDGE,"E6.bottom"),sQuery(id+"F41.wireOp",EDGE,"E6.top"),sQuery(id+"F41.wireOp",EDGE,"E6.left"),sQuery(id+"F41.wireOp",EDGE,"E6.right")])],"isStart":true});
            var Q3;
            Q3=makeQuery(id+"F42.opExtrude","SWEPT_FACE",FACE,{"disambiguationData":[OSD([sQuery(id+"F41.wireOp",EDGE,"E6.right")])]});
            fillet(context, id + "F43", {"entities" : qUnion([Q0, Q1, Q2, Q3]), "radius" : 20 * mm, "tangentPropagation" : true, "allowEdgeOverflow" : false});
        }
        {
            var Q0;
            Q0=qCreatedBy(makeId("Right.planeOp"),FACE);
            var sketch = newSketch(context, id + "F44", { "sketchPlane" : qUnion([Q0])});
            skLineSegment(sketch, "E7.bottom", {"start": v(256.56, 426.58) * mm, "end": v(132.08, 426.58) * mm});
            skLineSegment(sketch, "E7.top", {"start": v(256.56, 831.24) * mm, "end": v(132.08, 831.24) * mm});
            skLineSegment(sketch, "E7.left", {"start": v(256.56, 426.58) * mm, "end": v(256.56, 831.24) * mm});
            skLineSegment(sketch, "E7.right", {"start": v(132.08, 426.58) * mm, "end": v(132.08, 831.24) * mm});
            skSolve(sketch);
        }
        {
            var Q0;
            Q0=makeQuery(id+"F44.imprint","IMPRINT",FACE,{"disambiguationData":[TD([[makeQuery(id+"F44.imprint","IMPRINT",EDGE,{"derivedFrom":sQuery(id+"F44.wireOp",EDGE,"E7.bottom")}),-1.0]])]});
            extrude(context, id + "F45", {"entities" : qUnion([Q0]), "endBound" : BoundingType.SYMMETRIC, "depth" : 1200 * mm});
        }
        {
            var Q0;
            Q0=makeQuery(id+"F45.opExtrude","SWEPT_FACE",FACE,{"disambiguationData":[OSD([sQuery(id+"F44.wireOp",EDGE,"E7.top")])]});
            var Q1;
            Q1=makeQuery(id+"F45.opExtrude","CAP_FACE",FACE,{"disambiguationData":[OSD([sQuery(id+"F44.wireOp",EDGE,"E7.bottom"),sQuery(id+"F44.wireOp",EDGE,"E7.top"),sQuery(id+"F44.wireOp",EDGE,"E7.left"),sQuery(id+"F44.wireOp",EDGE,"E7.right")])],"isStart":false});
            var Q2;
            Q2=makeQuery(id+"F45.opExtrude","SWEPT_FACE",FACE,{"disambiguationData":[OSD([sQuery(id+"F44.wireOp",EDGE,"E7.right")])]});
            var Q3;
            Q3=makeQuery(id+"F45.opExtrude","CAP_FACE",FACE,{"disambiguationData":[OSD([sQuery(id+"F44.wireOp",EDGE,"E7.bottom"),sQuery(id+"F44.wireOp",EDGE,"E7.top"),sQuery(id+"F44.wireOp",EDGE,"E7.left"),sQuery(id+"F44.wireOp",EDGE,"E7.right")])],"isStart":true});
            fillet(context, id + "F46", {"entities" : qUnion([Q0, Q1, Q2, Q3]), "radius" : 20 * mm, "tangentPropagation" : true, "allowEdgeOverflow" : false});
        }
    });
